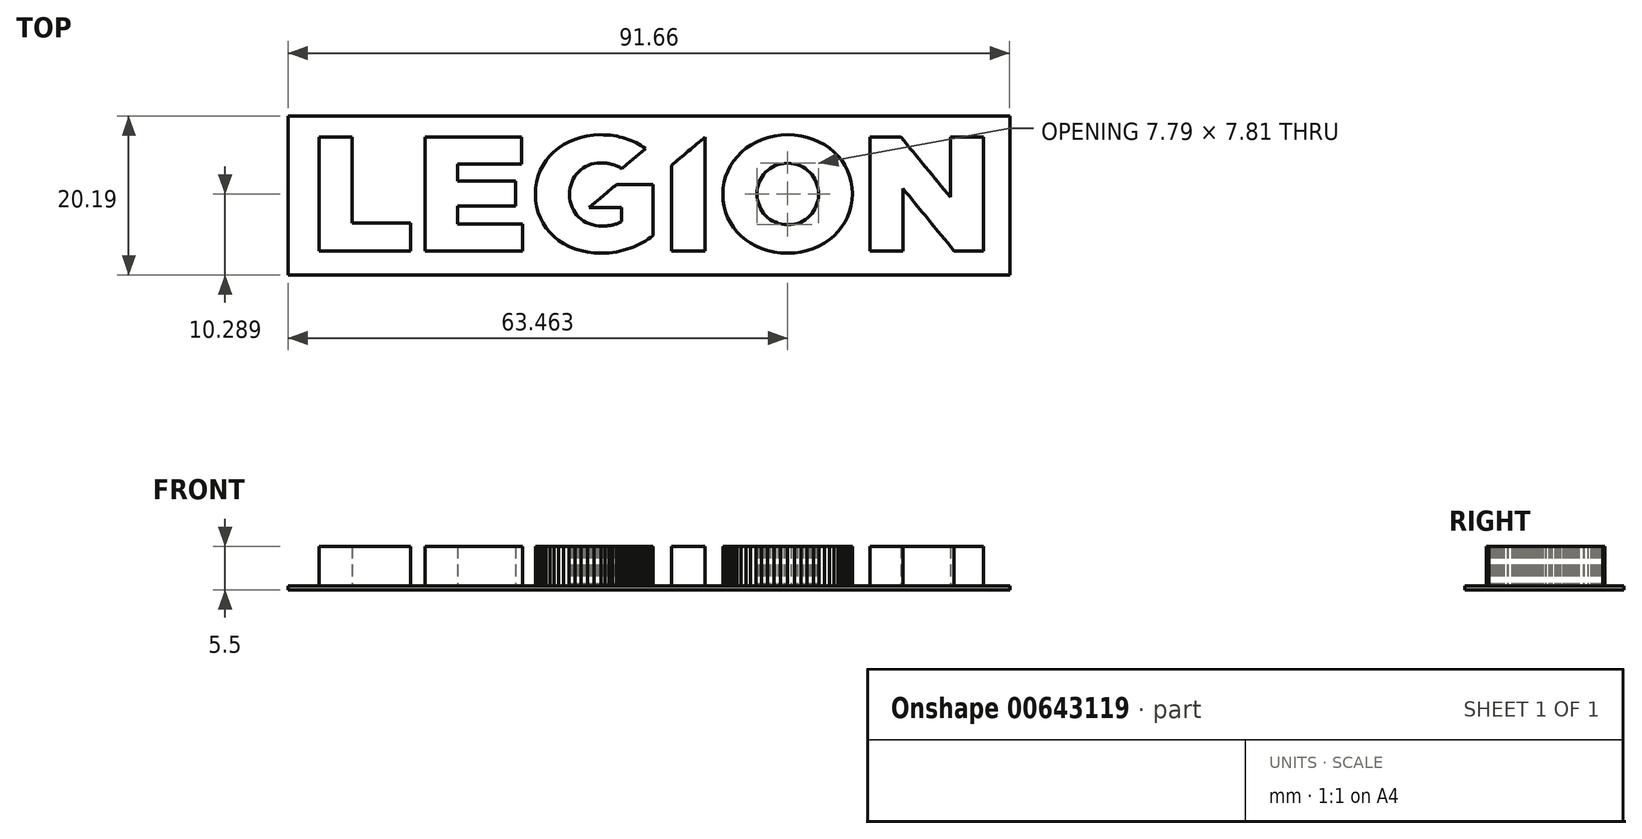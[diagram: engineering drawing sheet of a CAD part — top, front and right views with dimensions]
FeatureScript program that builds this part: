
annotation { "Feature Type Name" : "Feature", "Feature Type Description" : "" }
export const myFeature = defineFeature(function(context is Context, id is Id, definition is map)
    precondition{}
    {
        {
            var Q0;
            Q0=qCreatedBy(makeId("Top.planeOp"),FACE);
            var sketch = newSketch(context, id + "F0", { "sketchPlane" : qUnion([Q0])});
            skLineSegment(sketch, "E0", {"start": v(-42.2, 7.23) * mm, "end": v(-41.94, 7.23) * mm});
            skLineSegment(sketch, "E1", {"start": v(-41.94, 7.23) * mm, "end": v(-41.67, 7.23) * mm});
            skLineSegment(sketch, "E2", {"start": v(-41.67, 7.23) * mm, "end": v(-41.4, 7.23) * mm});
            skLineSegment(sketch, "E3", {"start": v(-41.4, 7.23) * mm, "end": v(-41.14, 7.23) * mm});
            skLineSegment(sketch, "E4", {"start": v(-41.14, 7.23) * mm, "end": v(-40.88, 7.23) * mm});
            skLineSegment(sketch, "E5", {"start": v(-40.88, 7.23) * mm, "end": v(-40.61, 7.23) * mm});
            skLineSegment(sketch, "E6", {"start": v(-40.61, 7.23) * mm, "end": v(-40.35, 7.23) * mm});
            skLineSegment(sketch, "E7", {"start": v(-40.35, 7.23) * mm, "end": v(-40.08, 7.23) * mm});
            skLineSegment(sketch, "E8", {"start": v(-40.08, 7.23) * mm, "end": v(-39.82, 7.23) * mm});
            skLineSegment(sketch, "E9", {"start": v(-39.82, 7.23) * mm, "end": v(-39.55, 7.23) * mm});
            skLineSegment(sketch, "E10", {"start": v(-39.55, 7.23) * mm, "end": v(-39.29, 7.23) * mm});
            skLineSegment(sketch, "E11", {"start": v(-39.29, 7.23) * mm, "end": v(-39.02, 7.23) * mm});
            skLineSegment(sketch, "E12", {"start": v(-39.02, 7.23) * mm, "end": v(-38.76, 7.23) * mm});
            skLineSegment(sketch, "E13", {"start": v(-38.76, 7.23) * mm, "end": v(-38.5, 7.23) * mm});
            skLineSegment(sketch, "E14", {"start": v(-38.5, 7.23) * mm, "end": v(-38.23, 7.23) * mm});
            skLineSegment(sketch, "E15", {"start": v(-38.23, 7.23) * mm, "end": v(-37.97, 7.23) * mm});
            skLineSegment(sketch, "E16", {"start": v(-37.97, 7.23) * mm, "end": v(-37.97, 6.55) * mm});
            skLineSegment(sketch, "E17", {"start": v(-37.97, 6.55) * mm, "end": v(-37.97, 5.86) * mm});
            skLineSegment(sketch, "E18", {"start": v(-37.97, 5.86) * mm, "end": v(-37.97, 5.18) * mm});
            skLineSegment(sketch, "E19", {"start": v(-37.97, 5.18) * mm, "end": v(-37.97, 4.5) * mm});
            skLineSegment(sketch, "E20", {"start": v(-37.97, 4.5) * mm, "end": v(-37.97, 3.81) * mm});
            skLineSegment(sketch, "E21", {"start": v(-37.97, 3.81) * mm, "end": v(-37.97, 3.13) * mm});
            skLineSegment(sketch, "E22", {"start": v(-37.97, 3.13) * mm, "end": v(-37.97, 2.44) * mm});
            skLineSegment(sketch, "E23", {"start": v(-37.97, 2.44) * mm, "end": v(-37.97, 1.76) * mm});
            skLineSegment(sketch, "E24", {"start": v(-37.97, 1.76) * mm, "end": v(-37.97, 1.07) * mm});
            skLineSegment(sketch, "E25", {"start": v(-37.97, 1.07) * mm, "end": v(-37.97, 0.39) * mm});
            skLineSegment(sketch, "E26", {"start": v(-37.97, 0.39) * mm, "end": v(-37.97, -0.3) * mm});
            skLineSegment(sketch, "E27", {"start": v(-37.97, -0.3) * mm, "end": v(-37.97, -0.98) * mm});
            skLineSegment(sketch, "E28", {"start": v(-37.97, -0.98) * mm, "end": v(-37.97, -1.67) * mm});
            skLineSegment(sketch, "E29", {"start": v(-37.97, -1.67) * mm, "end": v(-37.97, -2.35) * mm});
            skLineSegment(sketch, "E30", {"start": v(-37.97, -2.35) * mm, "end": v(-37.97, -3.04) * mm});
            skLineSegment(sketch, "E31", {"start": v(-37.97, -3.04) * mm, "end": v(-37.97, -3.72) * mm});
            skLineSegment(sketch, "E32", {"start": v(-37.97, -3.72) * mm, "end": v(-37.5, -3.72) * mm});
            skLineSegment(sketch, "E33", {"start": v(-37.5, -3.72) * mm, "end": v(-37.04, -3.72) * mm});
            skLineSegment(sketch, "E34", {"start": v(-37.04, -3.72) * mm, "end": v(-36.58, -3.72) * mm});
            skLineSegment(sketch, "E35", {"start": v(-36.58, -3.72) * mm, "end": v(-36.12, -3.72) * mm});
            skLineSegment(sketch, "E36", {"start": v(-36.12, -3.72) * mm, "end": v(-35.65, -3.72) * mm});
            skLineSegment(sketch, "E37", {"start": v(-35.65, -3.72) * mm, "end": v(-35.2, -3.72) * mm});
            skLineSegment(sketch, "E38", {"start": v(-35.2, -3.72) * mm, "end": v(-34.73, -3.72) * mm});
            skLineSegment(sketch, "E39", {"start": v(-34.73, -3.72) * mm, "end": v(-34.27, -3.72) * mm});
            skLineSegment(sketch, "E40", {"start": v(-34.27, -3.72) * mm, "end": v(-33.8, -3.72) * mm});
            skLineSegment(sketch, "E41", {"start": v(-33.8, -3.72) * mm, "end": v(-33.34, -3.72) * mm});
            skLineSegment(sketch, "E42", {"start": v(-33.34, -3.72) * mm, "end": v(-32.88, -3.72) * mm});
            skLineSegment(sketch, "E43", {"start": v(-32.88, -3.72) * mm, "end": v(-32.42, -3.72) * mm});
            skLineSegment(sketch, "E44", {"start": v(-32.42, -3.72) * mm, "end": v(-31.95, -3.72) * mm});
            skLineSegment(sketch, "E45", {"start": v(-31.95, -3.72) * mm, "end": v(-31.5, -3.72) * mm});
            skLineSegment(sketch, "E46", {"start": v(-31.5, -3.72) * mm, "end": v(-31.03, -3.72) * mm});
            skLineSegment(sketch, "E47", {"start": v(-31.03, -3.72) * mm, "end": v(-30.57, -3.72) * mm});
            skLineSegment(sketch, "E48", {"start": v(-30.57, -3.72) * mm, "end": v(-30.57, -3.94) * mm});
            skLineSegment(sketch, "E49", {"start": v(-30.57, -3.94) * mm, "end": v(-30.57, -4.16) * mm});
            skLineSegment(sketch, "E50", {"start": v(-30.57, -4.16) * mm, "end": v(-30.57, -4.38) * mm});
            skLineSegment(sketch, "E51", {"start": v(-30.57, -4.38) * mm, "end": v(-30.57, -4.6) * mm});
            skLineSegment(sketch, "E52", {"start": v(-30.57, -4.6) * mm, "end": v(-30.57, -4.82) * mm});
            skLineSegment(sketch, "E53", {"start": v(-30.57, -4.82) * mm, "end": v(-30.57, -5.04) * mm});
            skLineSegment(sketch, "E54", {"start": v(-30.57, -5.04) * mm, "end": v(-30.57, -5.26) * mm});
            skLineSegment(sketch, "E55", {"start": v(-30.57, -5.26) * mm, "end": v(-30.57, -5.48) * mm});
            skLineSegment(sketch, "E56", {"start": v(-30.57, -5.48) * mm, "end": v(-30.57, -5.7) * mm});
            skLineSegment(sketch, "E57", {"start": v(-30.57, -5.7) * mm, "end": v(-30.57, -5.92) * mm});
            skLineSegment(sketch, "E58", {"start": v(-30.57, -5.92) * mm, "end": v(-30.57, -6.14) * mm});
            skLineSegment(sketch, "E59", {"start": v(-30.57, -6.14) * mm, "end": v(-30.57, -6.36) * mm});
            skLineSegment(sketch, "E60", {"start": v(-30.57, -6.36) * mm, "end": v(-30.57, -6.58) * mm});
            skLineSegment(sketch, "E61", {"start": v(-30.57, -6.58) * mm, "end": v(-30.57, -6.8) * mm});
            skLineSegment(sketch, "E62", {"start": v(-30.57, -6.8) * mm, "end": v(-30.57, -7.01) * mm});
            skLineSegment(sketch, "E63", {"start": v(-30.57, -7.01) * mm, "end": v(-30.57, -7.23) * mm});
            skLineSegment(sketch, "E64", {"start": v(-30.57, -7.23) * mm, "end": v(-31.3, -7.23) * mm});
            skLineSegment(sketch, "E65", {"start": v(-31.3, -7.23) * mm, "end": v(-32.02, -7.23) * mm});
            skLineSegment(sketch, "E66", {"start": v(-32.02, -7.23) * mm, "end": v(-32.75, -7.23) * mm});
            skLineSegment(sketch, "E67", {"start": v(-32.75, -7.23) * mm, "end": v(-33.47, -7.23) * mm});
            skLineSegment(sketch, "E68", {"start": v(-33.47, -7.23) * mm, "end": v(-34.2, -7.23) * mm});
            skLineSegment(sketch, "E69", {"start": v(-34.2, -7.23) * mm, "end": v(-34.93, -7.23) * mm});
            skLineSegment(sketch, "E70", {"start": v(-34.93, -7.23) * mm, "end": v(-35.66, -7.23) * mm});
            skLineSegment(sketch, "E71", {"start": v(-35.66, -7.23) * mm, "end": v(-36.38, -7.23) * mm});
            skLineSegment(sketch, "E72", {"start": v(-36.38, -7.23) * mm, "end": v(-37.1, -7.23) * mm});
            skLineSegment(sketch, "E73", {"start": v(-37.1, -7.23) * mm, "end": v(-37.84, -7.23) * mm});
            skLineSegment(sketch, "E74", {"start": v(-37.84, -7.23) * mm, "end": v(-38.56, -7.23) * mm});
            skLineSegment(sketch, "E75", {"start": v(-38.56, -7.23) * mm, "end": v(-39.3, -7.23) * mm});
            skLineSegment(sketch, "E76", {"start": v(-39.3, -7.23) * mm, "end": v(-40.02, -7.23) * mm});
            skLineSegment(sketch, "E77", {"start": v(-40.02, -7.23) * mm, "end": v(-40.75, -7.23) * mm});
            skLineSegment(sketch, "E78", {"start": v(-40.75, -7.23) * mm, "end": v(-41.47, -7.23) * mm});
            skLineSegment(sketch, "E79", {"start": v(-41.47, -7.23) * mm, "end": v(-42.2, -7.23) * mm});
            skLineSegment(sketch, "E80", {"start": v(-42.2, -7.23) * mm, "end": v(-42.2, -6.33) * mm});
            skLineSegment(sketch, "E81", {"start": v(-42.2, -6.33) * mm, "end": v(-42.2, -5.43) * mm});
            skLineSegment(sketch, "E82", {"start": v(-42.2, -5.43) * mm, "end": v(-42.2, -4.52) * mm});
            skLineSegment(sketch, "E83", {"start": v(-42.2, -4.52) * mm, "end": v(-42.2, -3.62) * mm});
            skLineSegment(sketch, "E84", {"start": v(-42.2, -3.62) * mm, "end": v(-42.2, -2.71) * mm});
            skLineSegment(sketch, "E85", {"start": v(-42.2, -2.71) * mm, "end": v(-42.2, -1.8) * mm});
            skLineSegment(sketch, "E86", {"start": v(-42.2, -1.8) * mm, "end": v(-42.2, -0.9) * mm});
            skLineSegment(sketch, "E87", {"start": v(-42.2, -0.9) * mm, "end": v(-42.2, 0) * mm});
            skLineSegment(sketch, "E88", {"start": v(-42.2, 0) * mm, "end": v(-42.2, 0.9) * mm});
            skLineSegment(sketch, "E89", {"start": v(-42.2, 0.9) * mm, "end": v(-42.2, 1.8) * mm});
            skLineSegment(sketch, "E90", {"start": v(-42.2, 1.8) * mm, "end": v(-42.2, 2.71) * mm});
            skLineSegment(sketch, "E91", {"start": v(-42.2, 2.71) * mm, "end": v(-42.2, 3.62) * mm});
            skLineSegment(sketch, "E92", {"start": v(-42.2, 3.62) * mm, "end": v(-42.2, 4.52) * mm});
            skLineSegment(sketch, "E93", {"start": v(-42.2, 4.52) * mm, "end": v(-42.2, 5.43) * mm});
            skLineSegment(sketch, "E94", {"start": v(-42.2, 5.43) * mm, "end": v(-42.2, 6.33) * mm});
            skLineSegment(sketch, "E95", {"start": v(-42.2, 6.33) * mm, "end": v(-42.2, 7.23) * mm});
            skLineSegment(sketch, "E96", {"start": v(-28.75, 7.23) * mm, "end": v(-27.98, 7.23) * mm});
            skLineSegment(sketch, "E97", {"start": v(-27.98, 7.23) * mm, "end": v(-27.22, 7.23) * mm});
            skLineSegment(sketch, "E98", {"start": v(-27.22, 7.23) * mm, "end": v(-26.45, 7.23) * mm});
            skLineSegment(sketch, "E99", {"start": v(-26.45, 7.23) * mm, "end": v(-25.68, 7.23) * mm});
            skLineSegment(sketch, "E100", {"start": v(-25.68, 7.23) * mm, "end": v(-24.91, 7.23) * mm});
            skLineSegment(sketch, "E101", {"start": v(-24.91, 7.23) * mm, "end": v(-24.14, 7.23) * mm});
            skLineSegment(sketch, "E102", {"start": v(-24.14, 7.23) * mm, "end": v(-23.37, 7.23) * mm});
            skLineSegment(sketch, "E103", {"start": v(-23.37, 7.23) * mm, "end": v(-22.6, 7.23) * mm});
            skLineSegment(sketch, "E104", {"start": v(-22.6, 7.23) * mm, "end": v(-21.84, 7.23) * mm});
            skLineSegment(sketch, "E105", {"start": v(-21.84, 7.23) * mm, "end": v(-21.07, 7.23) * mm});
            skLineSegment(sketch, "E106", {"start": v(-21.07, 7.23) * mm, "end": v(-20.3, 7.23) * mm});
            skLineSegment(sketch, "E107", {"start": v(-20.3, 7.23) * mm, "end": v(-19.53, 7.23) * mm});
            skLineSegment(sketch, "E108", {"start": v(-19.53, 7.23) * mm, "end": v(-18.76, 7.23) * mm});
            skLineSegment(sketch, "E109", {"start": v(-18.76, 7.23) * mm, "end": v(-18, 7.23) * mm});
            skLineSegment(sketch, "E110", {"start": v(-18, 7.23) * mm, "end": v(-17.23, 7.23) * mm});
            skLineSegment(sketch, "E111", {"start": v(-17.23, 7.23) * mm, "end": v(-16.46, 7.23) * mm});
            skLineSegment(sketch, "E112", {"start": v(-16.46, 7.23) * mm, "end": v(-16.46, 7.02) * mm});
            skLineSegment(sketch, "E113", {"start": v(-16.46, 7.02) * mm, "end": v(-16.46, 6.8) * mm});
            skLineSegment(sketch, "E114", {"start": v(-16.46, 6.8) * mm, "end": v(-16.46, 6.6) * mm});
            skLineSegment(sketch, "E115", {"start": v(-16.46, 6.6) * mm, "end": v(-16.46, 6.38) * mm});
            skLineSegment(sketch, "E116", {"start": v(-16.46, 6.38) * mm, "end": v(-16.46, 6.17) * mm});
            skLineSegment(sketch, "E117", {"start": v(-16.46, 6.17) * mm, "end": v(-16.46, 5.96) * mm});
            skLineSegment(sketch, "E118", {"start": v(-16.46, 5.96) * mm, "end": v(-16.46, 5.74) * mm});
            skLineSegment(sketch, "E119", {"start": v(-16.46, 5.74) * mm, "end": v(-16.46, 5.53) * mm});
            skLineSegment(sketch, "E120", {"start": v(-16.46, 5.53) * mm, "end": v(-16.46, 5.32) * mm});
            skLineSegment(sketch, "E121", {"start": v(-16.46, 5.32) * mm, "end": v(-16.46, 5.1) * mm});
            skLineSegment(sketch, "E122", {"start": v(-16.46, 5.1) * mm, "end": v(-16.46, 4.89) * mm});
            skLineSegment(sketch, "E123", {"start": v(-16.46, 4.89) * mm, "end": v(-16.46, 4.68) * mm});
            skLineSegment(sketch, "E124", {"start": v(-16.46, 4.68) * mm, "end": v(-16.46, 4.46) * mm});
            skLineSegment(sketch, "E125", {"start": v(-16.46, 4.46) * mm, "end": v(-16.46, 4.25) * mm});
            skLineSegment(sketch, "E126", {"start": v(-16.46, 4.25) * mm, "end": v(-16.46, 4.04) * mm});
            skLineSegment(sketch, "E127", {"start": v(-16.46, 4.04) * mm, "end": v(-16.46, 3.82) * mm});
            skLineSegment(sketch, "E128", {"start": v(-16.46, 3.82) * mm, "end": v(-16.97, 3.82) * mm});
            skLineSegment(sketch, "E129", {"start": v(-16.97, 3.82) * mm, "end": v(-17.47, 3.82) * mm});
            skLineSegment(sketch, "E130", {"start": v(-17.47, 3.82) * mm, "end": v(-17.98, 3.82) * mm});
            skLineSegment(sketch, "E131", {"start": v(-17.98, 3.82) * mm, "end": v(-18.49, 3.82) * mm});
            skLineSegment(sketch, "E132", {"start": v(-18.49, 3.82) * mm, "end": v(-19, 3.82) * mm});
            skLineSegment(sketch, "E133", {"start": v(-19, 3.82) * mm, "end": v(-19.5, 3.82) * mm});
            skLineSegment(sketch, "E134", {"start": v(-19.5, 3.82) * mm, "end": v(-20, 3.82) * mm});
            skLineSegment(sketch, "E135", {"start": v(-20, 3.82) * mm, "end": v(-20.51, 3.82) * mm});
            skLineSegment(sketch, "E136", {"start": v(-20.51, 3.82) * mm, "end": v(-21.02, 3.82) * mm});
            skLineSegment(sketch, "E137", {"start": v(-21.02, 3.82) * mm, "end": v(-21.52, 3.82) * mm});
            skLineSegment(sketch, "E138", {"start": v(-21.52, 3.82) * mm, "end": v(-22.03, 3.82) * mm});
            skLineSegment(sketch, "E139", {"start": v(-22.03, 3.82) * mm, "end": v(-22.54, 3.82) * mm});
            skLineSegment(sketch, "E140", {"start": v(-22.54, 3.82) * mm, "end": v(-23.04, 3.82) * mm});
            skLineSegment(sketch, "E141", {"start": v(-23.04, 3.82) * mm, "end": v(-23.55, 3.82) * mm});
            skLineSegment(sketch, "E142", {"start": v(-23.55, 3.82) * mm, "end": v(-24.06, 3.82) * mm});
            skLineSegment(sketch, "E143", {"start": v(-24.06, 3.82) * mm, "end": v(-24.56, 3.82) * mm});
            skLineSegment(sketch, "E144", {"start": v(-24.56, 3.82) * mm, "end": v(-24.56, 3.69) * mm});
            skLineSegment(sketch, "E145", {"start": v(-24.56, 3.69) * mm, "end": v(-24.56, 3.55) * mm});
            skLineSegment(sketch, "E146", {"start": v(-24.56, 3.55) * mm, "end": v(-24.56, 3.41) * mm});
            skLineSegment(sketch, "E147", {"start": v(-24.56, 3.41) * mm, "end": v(-24.56, 3.28) * mm});
            skLineSegment(sketch, "E148", {"start": v(-24.56, 3.28) * mm, "end": v(-24.56, 3.14) * mm});
            skLineSegment(sketch, "E149", {"start": v(-24.56, 3.14) * mm, "end": v(-24.56, 3) * mm});
            skLineSegment(sketch, "E150", {"start": v(-24.56, 3) * mm, "end": v(-24.56, 2.87) * mm});
            skLineSegment(sketch, "E151", {"start": v(-24.56, 2.87) * mm, "end": v(-24.56, 2.73) * mm});
            skLineSegment(sketch, "E152", {"start": v(-24.56, 2.73) * mm, "end": v(-24.56, 2.6) * mm});
            skLineSegment(sketch, "E153", {"start": v(-24.56, 2.6) * mm, "end": v(-24.56, 2.45) * mm});
            skLineSegment(sketch, "E154", {"start": v(-24.56, 2.45) * mm, "end": v(-24.56, 2.32) * mm});
            skLineSegment(sketch, "E155", {"start": v(-24.56, 2.32) * mm, "end": v(-24.56, 2.18) * mm});
            skLineSegment(sketch, "E156", {"start": v(-24.56, 2.18) * mm, "end": v(-24.56, 2.04) * mm});
            skLineSegment(sketch, "E157", {"start": v(-24.56, 2.04) * mm, "end": v(-24.56, 1.9) * mm});
            skLineSegment(sketch, "E158", {"start": v(-24.56, 1.9) * mm, "end": v(-24.56, 1.77) * mm});
            skLineSegment(sketch, "E159", {"start": v(-24.56, 1.77) * mm, "end": v(-24.56, 1.63) * mm});
            skLineSegment(sketch, "E160", {"start": v(-24.56, 1.63) * mm, "end": v(-24.1, 1.63) * mm});
            skLineSegment(sketch, "E161", {"start": v(-24.1, 1.63) * mm, "end": v(-23.64, 1.63) * mm});
            skLineSegment(sketch, "E162", {"start": v(-23.64, 1.63) * mm, "end": v(-23.19, 1.63) * mm});
            skLineSegment(sketch, "E163", {"start": v(-23.19, 1.63) * mm, "end": v(-22.73, 1.63) * mm});
            skLineSegment(sketch, "E164", {"start": v(-22.73, 1.63) * mm, "end": v(-22.27, 1.63) * mm});
            skLineSegment(sketch, "E165", {"start": v(-22.27, 1.63) * mm, "end": v(-21.81, 1.63) * mm});
            skLineSegment(sketch, "E166", {"start": v(-21.81, 1.63) * mm, "end": v(-21.35, 1.63) * mm});
            skLineSegment(sketch, "E167", {"start": v(-21.35, 1.63) * mm, "end": v(-20.9, 1.63) * mm});
            skLineSegment(sketch, "E168", {"start": v(-20.9, 1.63) * mm, "end": v(-20.43, 1.63) * mm});
            skLineSegment(sketch, "E169", {"start": v(-20.43, 1.63) * mm, "end": v(-19.98, 1.63) * mm});
            skLineSegment(sketch, "E170", {"start": v(-19.98, 1.63) * mm, "end": v(-19.52, 1.63) * mm});
            skLineSegment(sketch, "E171", {"start": v(-19.52, 1.63) * mm, "end": v(-19.06, 1.63) * mm});
            skLineSegment(sketch, "E172", {"start": v(-19.06, 1.63) * mm, "end": v(-18.6, 1.63) * mm});
            skLineSegment(sketch, "E173", {"start": v(-18.6, 1.63) * mm, "end": v(-18.14, 1.63) * mm});
            skLineSegment(sketch, "E174", {"start": v(-18.14, 1.63) * mm, "end": v(-17.68, 1.63) * mm});
            skLineSegment(sketch, "E175", {"start": v(-17.68, 1.63) * mm, "end": v(-17.23, 1.63) * mm});
            skLineSegment(sketch, "E176", {"start": v(-17.23, 1.63) * mm, "end": v(-17.23, 1.44) * mm});
            skLineSegment(sketch, "E177", {"start": v(-17.23, 1.44) * mm, "end": v(-17.23, 1.24) * mm});
            skLineSegment(sketch, "E178", {"start": v(-17.23, 1.24) * mm, "end": v(-17.23, 1.04) * mm});
            skLineSegment(sketch, "E179", {"start": v(-17.23, 1.04) * mm, "end": v(-17.23, 0.84) * mm});
            skLineSegment(sketch, "E180", {"start": v(-17.23, 0.84) * mm, "end": v(-17.23, 0.64) * mm});
            skLineSegment(sketch, "E181", {"start": v(-17.23, 0.64) * mm, "end": v(-17.23, 0.45) * mm});
            skLineSegment(sketch, "E182", {"start": v(-17.23, 0.45) * mm, "end": v(-17.23, 0.25) * mm});
            skLineSegment(sketch, "E183", {"start": v(-17.23, 0.25) * mm, "end": v(-17.23, 0.05) * mm});
            skLineSegment(sketch, "E184", {"start": v(-17.23, 0.05) * mm, "end": v(-17.23, -0.15) * mm});
            skLineSegment(sketch, "E185", {"start": v(-17.23, -0.15) * mm, "end": v(-17.23, -0.34) * mm});
            skLineSegment(sketch, "E186", {"start": v(-17.23, -0.34) * mm, "end": v(-17.23, -0.54) * mm});
            skLineSegment(sketch, "E187", {"start": v(-17.23, -0.54) * mm, "end": v(-17.23, -0.74) * mm});
            skLineSegment(sketch, "E188", {"start": v(-17.23, -0.74) * mm, "end": v(-17.23, -0.94) * mm});
            skLineSegment(sketch, "E189", {"start": v(-17.23, -0.94) * mm, "end": v(-17.23, -1.13) * mm});
            skLineSegment(sketch, "E190", {"start": v(-17.23, -1.13) * mm, "end": v(-17.23, -1.33) * mm});
            skLineSegment(sketch, "E191", {"start": v(-17.23, -1.33) * mm, "end": v(-17.23, -1.53) * mm});
            skLineSegment(sketch, "E192", {"start": v(-17.23, -1.53) * mm, "end": v(-17.68, -1.53) * mm});
            skLineSegment(sketch, "E193", {"start": v(-17.68, -1.53) * mm, "end": v(-18.14, -1.53) * mm});
            skLineSegment(sketch, "E194", {"start": v(-18.14, -1.53) * mm, "end": v(-18.6, -1.53) * mm});
            skLineSegment(sketch, "E195", {"start": v(-18.6, -1.53) * mm, "end": v(-19.06, -1.53) * mm});
            skLineSegment(sketch, "E196", {"start": v(-19.06, -1.53) * mm, "end": v(-19.52, -1.53) * mm});
            skLineSegment(sketch, "E197", {"start": v(-19.52, -1.53) * mm, "end": v(-19.98, -1.53) * mm});
            skLineSegment(sketch, "E198", {"start": v(-19.98, -1.53) * mm, "end": v(-20.43, -1.53) * mm});
            skLineSegment(sketch, "E199", {"start": v(-20.43, -1.53) * mm, "end": v(-20.9, -1.53) * mm});
            skLineSegment(sketch, "E200", {"start": v(-20.9, -1.53) * mm, "end": v(-21.35, -1.53) * mm});
            skLineSegment(sketch, "E201", {"start": v(-21.35, -1.53) * mm, "end": v(-21.81, -1.53) * mm});
            skLineSegment(sketch, "E202", {"start": v(-21.81, -1.53) * mm, "end": v(-22.27, -1.53) * mm});
            skLineSegment(sketch, "E203", {"start": v(-22.27, -1.53) * mm, "end": v(-22.73, -1.53) * mm});
            skLineSegment(sketch, "E204", {"start": v(-22.73, -1.53) * mm, "end": v(-23.19, -1.53) * mm});
            skLineSegment(sketch, "E205", {"start": v(-23.19, -1.53) * mm, "end": v(-23.64, -1.53) * mm});
            skLineSegment(sketch, "E206", {"start": v(-23.64, -1.53) * mm, "end": v(-24.1, -1.53) * mm});
            skLineSegment(sketch, "E207", {"start": v(-24.1, -1.53) * mm, "end": v(-24.56, -1.53) * mm});
            skLineSegment(sketch, "E208", {"start": v(-24.56, -1.53) * mm, "end": v(-24.56, -1.67) * mm});
            skLineSegment(sketch, "E209", {"start": v(-24.56, -1.67) * mm, "end": v(-24.56, -1.82) * mm});
            skLineSegment(sketch, "E210", {"start": v(-24.56, -1.82) * mm, "end": v(-24.56, -1.96) * mm});
            skLineSegment(sketch, "E211", {"start": v(-24.56, -1.96) * mm, "end": v(-24.56, -2.1) * mm});
            skLineSegment(sketch, "E212", {"start": v(-24.56, -2.1) * mm, "end": v(-24.56, -2.25) * mm});
            skLineSegment(sketch, "E213", {"start": v(-24.56, -2.25) * mm, "end": v(-24.56, -2.39) * mm});
            skLineSegment(sketch, "E214", {"start": v(-24.56, -2.39) * mm, "end": v(-24.56, -2.53) * mm});
            skLineSegment(sketch, "E215", {"start": v(-24.56, -2.53) * mm, "end": v(-24.56, -2.68) * mm});
            skLineSegment(sketch, "E216", {"start": v(-24.56, -2.68) * mm, "end": v(-24.56, -2.82) * mm});
            skLineSegment(sketch, "E217", {"start": v(-24.56, -2.82) * mm, "end": v(-24.56, -2.96) * mm});
            skLineSegment(sketch, "E218", {"start": v(-24.56, -2.96) * mm, "end": v(-24.56, -3.1) * mm});
            skLineSegment(sketch, "E219", {"start": v(-24.56, -3.1) * mm, "end": v(-24.56, -3.25) * mm});
            skLineSegment(sketch, "E220", {"start": v(-24.56, -3.25) * mm, "end": v(-24.56, -3.4) * mm});
            skLineSegment(sketch, "E221", {"start": v(-24.56, -3.4) * mm, "end": v(-24.56, -3.54) * mm});
            skLineSegment(sketch, "E222", {"start": v(-24.56, -3.54) * mm, "end": v(-24.56, -3.68) * mm});
            skLineSegment(sketch, "E223", {"start": v(-24.56, -3.68) * mm, "end": v(-24.56, -3.82) * mm});
            skLineSegment(sketch, "E224", {"start": v(-24.56, -3.82) * mm, "end": v(-24.05, -3.82) * mm});
            skLineSegment(sketch, "E225", {"start": v(-24.05, -3.82) * mm, "end": v(-23.54, -3.82) * mm});
            skLineSegment(sketch, "E226", {"start": v(-23.54, -3.82) * mm, "end": v(-23.02, -3.82) * mm});
            skLineSegment(sketch, "E227", {"start": v(-23.02, -3.82) * mm, "end": v(-22.5, -3.82) * mm});
            skLineSegment(sketch, "E228", {"start": v(-22.5, -3.82) * mm, "end": v(-22, -3.82) * mm});
            skLineSegment(sketch, "E229", {"start": v(-22, -3.82) * mm, "end": v(-21.48, -3.82) * mm});
            skLineSegment(sketch, "E230", {"start": v(-21.48, -3.82) * mm, "end": v(-20.97, -3.82) * mm});
            skLineSegment(sketch, "E231", {"start": v(-20.97, -3.82) * mm, "end": v(-20.46, -3.82) * mm});
            skLineSegment(sketch, "E232", {"start": v(-20.46, -3.82) * mm, "end": v(-19.94, -3.82) * mm});
            skLineSegment(sketch, "E233", {"start": v(-19.94, -3.82) * mm, "end": v(-19.43, -3.82) * mm});
            skLineSegment(sketch, "E234", {"start": v(-19.43, -3.82) * mm, "end": v(-18.92, -3.82) * mm});
            skLineSegment(sketch, "E235", {"start": v(-18.92, -3.82) * mm, "end": v(-18.4, -3.82) * mm});
            skLineSegment(sketch, "E236", {"start": v(-18.4, -3.82) * mm, "end": v(-17.9, -3.82) * mm});
            skLineSegment(sketch, "E237", {"start": v(-17.9, -3.82) * mm, "end": v(-17.38, -3.82) * mm});
            skLineSegment(sketch, "E238", {"start": v(-17.38, -3.82) * mm, "end": v(-16.87, -3.82) * mm});
            skLineSegment(sketch, "E239", {"start": v(-16.87, -3.82) * mm, "end": v(-16.35, -3.82) * mm});
            skLineSegment(sketch, "E240", {"start": v(-16.35, -3.82) * mm, "end": v(-16.35, -4.04) * mm});
            skLineSegment(sketch, "E241", {"start": v(-16.35, -4.04) * mm, "end": v(-16.35, -4.25) * mm});
            skLineSegment(sketch, "E242", {"start": v(-16.35, -4.25) * mm, "end": v(-16.35, -4.46) * mm});
            skLineSegment(sketch, "E243", {"start": v(-16.35, -4.46) * mm, "end": v(-16.35, -4.68) * mm});
            skLineSegment(sketch, "E244", {"start": v(-16.35, -4.68) * mm, "end": v(-16.35, -4.89) * mm});
            skLineSegment(sketch, "E245", {"start": v(-16.35, -4.89) * mm, "end": v(-16.35, -5.1) * mm});
            skLineSegment(sketch, "E246", {"start": v(-16.35, -5.1) * mm, "end": v(-16.35, -5.32) * mm});
            skLineSegment(sketch, "E247", {"start": v(-16.35, -5.32) * mm, "end": v(-16.35, -5.53) * mm});
            skLineSegment(sketch, "E248", {"start": v(-16.35, -5.53) * mm, "end": v(-16.35, -5.74) * mm});
            skLineSegment(sketch, "E249", {"start": v(-16.35, -5.74) * mm, "end": v(-16.35, -5.96) * mm});
            skLineSegment(sketch, "E250", {"start": v(-16.35, -5.96) * mm, "end": v(-16.35, -6.17) * mm});
            skLineSegment(sketch, "E251", {"start": v(-16.35, -6.17) * mm, "end": v(-16.35, -6.38) * mm});
            skLineSegment(sketch, "E252", {"start": v(-16.35, -6.38) * mm, "end": v(-16.35, -6.6) * mm});
            skLineSegment(sketch, "E253", {"start": v(-16.35, -6.6) * mm, "end": v(-16.35, -6.8) * mm});
            skLineSegment(sketch, "E254", {"start": v(-16.35, -6.8) * mm, "end": v(-16.35, -7.02) * mm});
            skLineSegment(sketch, "E255", {"start": v(-16.35, -7.02) * mm, "end": v(-16.35, -7.23) * mm});
            skLineSegment(sketch, "E256", {"start": v(-16.35, -7.23) * mm, "end": v(-17.13, -7.23) * mm});
            skLineSegment(sketch, "E257", {"start": v(-17.13, -7.23) * mm, "end": v(-17.9, -7.23) * mm});
            skLineSegment(sketch, "E258", {"start": v(-17.9, -7.23) * mm, "end": v(-18.68, -7.23) * mm});
            skLineSegment(sketch, "E259", {"start": v(-18.68, -7.23) * mm, "end": v(-19.45, -7.23) * mm});
            skLineSegment(sketch, "E260", {"start": v(-19.45, -7.23) * mm, "end": v(-20.23, -7.23) * mm});
            skLineSegment(sketch, "E261", {"start": v(-20.23, -7.23) * mm, "end": v(-21, -7.23) * mm});
            skLineSegment(sketch, "E262", {"start": v(-21, -7.23) * mm, "end": v(-21.78, -7.23) * mm});
            skLineSegment(sketch, "E263", {"start": v(-21.78, -7.23) * mm, "end": v(-22.55, -7.23) * mm});
            skLineSegment(sketch, "E264", {"start": v(-22.55, -7.23) * mm, "end": v(-23.33, -7.23) * mm});
            skLineSegment(sketch, "E265", {"start": v(-23.33, -7.23) * mm, "end": v(-24.1, -7.23) * mm});
            skLineSegment(sketch, "E266", {"start": v(-24.1, -7.23) * mm, "end": v(-24.88, -7.23) * mm});
            skLineSegment(sketch, "E267", {"start": v(-24.88, -7.23) * mm, "end": v(-25.65, -7.23) * mm});
            skLineSegment(sketch, "E268", {"start": v(-25.65, -7.23) * mm, "end": v(-26.43, -7.23) * mm});
            skLineSegment(sketch, "E269", {"start": v(-26.43, -7.23) * mm, "end": v(-27.2, -7.23) * mm});
            skLineSegment(sketch, "E270", {"start": v(-27.2, -7.23) * mm, "end": v(-27.98, -7.23) * mm});
            skLineSegment(sketch, "E271", {"start": v(-27.98, -7.23) * mm, "end": v(-28.75, -7.23) * mm});
            skLineSegment(sketch, "E272", {"start": v(-28.75, -7.23) * mm, "end": v(-28.75, -6.33) * mm});
            skLineSegment(sketch, "E273", {"start": v(-28.75, -6.33) * mm, "end": v(-28.75, -5.43) * mm});
            skLineSegment(sketch, "E274", {"start": v(-28.75, -5.43) * mm, "end": v(-28.75, -4.52) * mm});
            skLineSegment(sketch, "E275", {"start": v(-28.75, -4.52) * mm, "end": v(-28.75, -3.62) * mm});
            skLineSegment(sketch, "E276", {"start": v(-28.75, -3.62) * mm, "end": v(-28.75, -2.71) * mm});
            skLineSegment(sketch, "E277", {"start": v(-28.75, -2.71) * mm, "end": v(-28.75, -1.8) * mm});
            skLineSegment(sketch, "E278", {"start": v(-28.75, -1.8) * mm, "end": v(-28.75, -0.9) * mm});
            skLineSegment(sketch, "E279", {"start": v(-28.75, -0.9) * mm, "end": v(-28.75, 0) * mm});
            skLineSegment(sketch, "E280", {"start": v(-28.75, 0) * mm, "end": v(-28.75, 0.9) * mm});
            skLineSegment(sketch, "E281", {"start": v(-28.75, 0.9) * mm, "end": v(-28.75, 1.8) * mm});
            skLineSegment(sketch, "E282", {"start": v(-28.75, 1.8) * mm, "end": v(-28.75, 2.71) * mm});
            skLineSegment(sketch, "E283", {"start": v(-28.75, 2.71) * mm, "end": v(-28.75, 3.62) * mm});
            skLineSegment(sketch, "E284", {"start": v(-28.75, 3.62) * mm, "end": v(-28.75, 4.52) * mm});
            skLineSegment(sketch, "E285", {"start": v(-28.75, 4.52) * mm, "end": v(-28.75, 5.43) * mm});
            skLineSegment(sketch, "E286", {"start": v(-28.75, 5.43) * mm, "end": v(-28.75, 6.33) * mm});
            skLineSegment(sketch, "E287", {"start": v(-28.75, 6.33) * mm, "end": v(-28.75, 7.23) * mm});
            skLineSegment(sketch, "E288", {"start": v(21.24, -0.04) * mm, "end": v(21.24, -0.04) * mm});
            skLineSegment(sketch, "E289", {"start": v(21.24, -0.04) * mm, "end": v(21.24, -0.03) * mm});
            skLineSegment(sketch, "E290", {"start": v(21.24, -0.03) * mm, "end": v(21.24, -0.03) * mm});
            skLineSegment(sketch, "E291", {"start": v(21.24, -0.03) * mm, "end": v(21.24, -0.02) * mm});
            skLineSegment(sketch, "E292", {"start": v(21.24, -0.02) * mm, "end": v(21.24, -0.02) * mm});
            skLineSegment(sketch, "E293", {"start": v(21.24, -0.02) * mm, "end": v(21.24, -0.01) * mm});
            skLineSegment(sketch, "E294", {"start": v(21.24, -0.01) * mm, "end": v(21.24, -0.01) * mm});
            skLineSegment(sketch, "E295", {"start": v(21.24, -0.01) * mm, "end": v(21.24, 0) * mm});
            skLineSegment(sketch, "E296", {"start": v(21.24, 0) * mm, "end": v(21.24, 0) * mm});
            skLineSegment(sketch, "E297", {"start": v(21.24, 0) * mm, "end": v(21.22, 0.39) * mm});
            skLineSegment(sketch, "E298", {"start": v(21.22, 0.39) * mm, "end": v(21.17, 0.77) * mm});
            skLineSegment(sketch, "E299", {"start": v(21.17, 0.77) * mm, "end": v(21.08, 1.14) * mm});
            skLineSegment(sketch, "E300", {"start": v(21.08, 1.14) * mm, "end": v(20.96, 1.5) * mm});
            skLineSegment(sketch, "E301", {"start": v(20.96, 1.5) * mm, "end": v(20.8, 1.83) * mm});
            skLineSegment(sketch, "E302", {"start": v(20.8, 1.83) * mm, "end": v(20.61, 2.15) * mm});
            skLineSegment(sketch, "E303", {"start": v(20.61, 2.15) * mm, "end": v(20.4, 2.46) * mm});
            skLineSegment(sketch, "E304", {"start": v(20.4, 2.46) * mm, "end": v(20.15, 2.74) * mm});
            skLineSegment(sketch, "E305", {"start": v(20.15, 2.74) * mm, "end": v(19.88, 3) * mm});
            skLineSegment(sketch, "E306", {"start": v(19.88, 3) * mm, "end": v(19.58, 3.22) * mm});
            skLineSegment(sketch, "E307", {"start": v(19.58, 3.22) * mm, "end": v(19.26, 3.42) * mm});
            skLineSegment(sketch, "E308", {"start": v(19.26, 3.42) * mm, "end": v(18.91, 3.59) * mm});
            skLineSegment(sketch, "E309", {"start": v(18.91, 3.59) * mm, "end": v(18.54, 3.72) * mm});
            skLineSegment(sketch, "E310", {"start": v(18.54, 3.72) * mm, "end": v(18.15, 3.82) * mm});
            skLineSegment(sketch, "E311", {"start": v(18.15, 3.82) * mm, "end": v(17.74, 3.88) * mm});
            skLineSegment(sketch, "E312", {"start": v(17.74, 3.88) * mm, "end": v(17.3, 3.9) * mm});
            skLineSegment(sketch, "E313", {"start": v(17.3, 3.9) * mm, "end": v(16.88, 3.89) * mm});
            skLineSegment(sketch, "E314", {"start": v(16.88, 3.89) * mm, "end": v(16.48, 3.83) * mm});
            skLineSegment(sketch, "E315", {"start": v(16.48, 3.83) * mm, "end": v(16.1, 3.73) * mm});
            skLineSegment(sketch, "E316", {"start": v(16.1, 3.73) * mm, "end": v(15.73, 3.6) * mm});
            skLineSegment(sketch, "E317", {"start": v(15.73, 3.6) * mm, "end": v(15.39, 3.43) * mm});
            skLineSegment(sketch, "E318", {"start": v(15.39, 3.43) * mm, "end": v(15.07, 3.23) * mm});
            skLineSegment(sketch, "E319", {"start": v(15.07, 3.23) * mm, "end": v(14.78, 3) * mm});
            skLineSegment(sketch, "E320", {"start": v(14.78, 3) * mm, "end": v(14.51, 2.76) * mm});
            skLineSegment(sketch, "E321", {"start": v(14.51, 2.76) * mm, "end": v(14.27, 2.48) * mm});
            skLineSegment(sketch, "E322", {"start": v(14.27, 2.48) * mm, "end": v(14.06, 2.18) * mm});
            skLineSegment(sketch, "E323", {"start": v(14.06, 2.18) * mm, "end": v(13.88, 1.86) * mm});
            skLineSegment(sketch, "E324", {"start": v(13.88, 1.86) * mm, "end": v(13.73, 1.53) * mm});
            skLineSegment(sketch, "E325", {"start": v(13.73, 1.53) * mm, "end": v(13.6, 1.17) * mm});
            skLineSegment(sketch, "E326", {"start": v(13.6, 1.17) * mm, "end": v(13.52, 0.8) * mm});
            skLineSegment(sketch, "E327", {"start": v(13.52, 0.8) * mm, "end": v(13.46, 0.43) * mm});
            skLineSegment(sketch, "E328", {"start": v(13.46, 0.43) * mm, "end": v(13.45, 0.04) * mm});
            skLineSegment(sketch, "E329", {"start": v(13.45, 0.04) * mm, "end": v(13.45, 0.04) * mm});
            skLineSegment(sketch, "E330", {"start": v(13.45, 0.04) * mm, "end": v(13.45, 0.03) * mm});
            skLineSegment(sketch, "E331", {"start": v(13.45, 0.03) * mm, "end": v(13.45, 0.03) * mm});
            skLineSegment(sketch, "E332", {"start": v(13.45, 0.03) * mm, "end": v(13.45, 0.02) * mm});
            skLineSegment(sketch, "E333", {"start": v(13.45, 0.02) * mm, "end": v(13.45, 0.02) * mm});
            skLineSegment(sketch, "E334", {"start": v(13.45, 0.02) * mm, "end": v(13.45, 0.01) * mm});
            skLineSegment(sketch, "E335", {"start": v(13.45, 0.01) * mm, "end": v(13.45, 0) * mm});
            skLineSegment(sketch, "E336", {"start": v(13.45, 0) * mm, "end": v(13.45, 0) * mm});
            skLineSegment(sketch, "E337", {"start": v(13.45, 0) * mm, "end": v(13.47, -0.39) * mm});
            skLineSegment(sketch, "E338", {"start": v(13.47, -0.39) * mm, "end": v(13.52, -0.77) * mm});
            skLineSegment(sketch, "E339", {"start": v(13.52, -0.77) * mm, "end": v(13.6, -1.14) * mm});
            skLineSegment(sketch, "E340", {"start": v(13.6, -1.14) * mm, "end": v(13.73, -1.5) * mm});
            skLineSegment(sketch, "E341", {"start": v(13.73, -1.5) * mm, "end": v(13.89, -1.83) * mm});
            skLineSegment(sketch, "E342", {"start": v(13.89, -1.83) * mm, "end": v(14.07, -2.15) * mm});
            skLineSegment(sketch, "E343", {"start": v(14.07, -2.15) * mm, "end": v(14.29, -2.46) * mm});
            skLineSegment(sketch, "E344", {"start": v(14.29, -2.46) * mm, "end": v(14.53, -2.74) * mm});
            skLineSegment(sketch, "E345", {"start": v(14.53, -2.74) * mm, "end": v(14.8, -3) * mm});
            skLineSegment(sketch, "E346", {"start": v(14.8, -3) * mm, "end": v(15.1, -3.22) * mm});
            skLineSegment(sketch, "E347", {"start": v(15.1, -3.22) * mm, "end": v(15.42, -3.42) * mm});
            skLineSegment(sketch, "E348", {"start": v(15.42, -3.42) * mm, "end": v(15.77, -3.6) * mm});
            skLineSegment(sketch, "E349", {"start": v(15.77, -3.6) * mm, "end": v(16.14, -3.73) * mm});
            skLineSegment(sketch, "E350", {"start": v(16.14, -3.73) * mm, "end": v(16.52, -3.83) * mm});
            skLineSegment(sketch, "E351", {"start": v(16.52, -3.83) * mm, "end": v(16.93, -3.89) * mm});
            skLineSegment(sketch, "E352", {"start": v(16.93, -3.89) * mm, "end": v(17.35, -3.9) * mm});
            skLineSegment(sketch, "E353", {"start": v(17.35, -3.9) * mm, "end": v(17.78, -3.89) * mm});
            skLineSegment(sketch, "E354", {"start": v(17.78, -3.89) * mm, "end": v(18.2, -3.83) * mm});
            skLineSegment(sketch, "E355", {"start": v(18.2, -3.83) * mm, "end": v(18.58, -3.73) * mm});
            skLineSegment(sketch, "E356", {"start": v(18.58, -3.73) * mm, "end": v(18.95, -3.6) * mm});
            skLineSegment(sketch, "E357", {"start": v(18.95, -3.6) * mm, "end": v(19.3, -3.43) * mm});
            skLineSegment(sketch, "E358", {"start": v(19.3, -3.43) * mm, "end": v(19.61, -3.24) * mm});
            skLineSegment(sketch, "E359", {"start": v(19.61, -3.24) * mm, "end": v(19.9, -3) * mm});
            skLineSegment(sketch, "E360", {"start": v(19.9, -3) * mm, "end": v(20.17, -2.76) * mm});
            skLineSegment(sketch, "E361", {"start": v(20.17, -2.76) * mm, "end": v(20.41, -2.48) * mm});
            skLineSegment(sketch, "E362", {"start": v(20.41, -2.48) * mm, "end": v(20.63, -2.18) * mm});
            skLineSegment(sketch, "E363", {"start": v(20.63, -2.18) * mm, "end": v(20.8, -1.86) * mm});
            skLineSegment(sketch, "E364", {"start": v(20.8, -1.86) * mm, "end": v(20.96, -1.53) * mm});
            skLineSegment(sketch, "E365", {"start": v(20.96, -1.53) * mm, "end": v(21.08, -1.17) * mm});
            skLineSegment(sketch, "E366", {"start": v(21.08, -1.17) * mm, "end": v(21.17, -0.8) * mm});
            skLineSegment(sketch, "E367", {"start": v(21.17, -0.8) * mm, "end": v(21.22, -0.43) * mm});
            skLineSegment(sketch, "E368", {"start": v(21.22, -0.43) * mm, "end": v(21.24, -0.04) * mm});
            skLineSegment(sketch, "E369", {"start": v(9.1, -0.04) * mm, "end": v(9.1, -0.04) * mm});
            skLineSegment(sketch, "E370", {"start": v(9.1, -0.04) * mm, "end": v(9.1, -0.03) * mm});
            skLineSegment(sketch, "E371", {"start": v(9.1, -0.03) * mm, "end": v(9.1, -0.03) * mm});
            skLineSegment(sketch, "E372", {"start": v(9.1, -0.03) * mm, "end": v(9.1, -0.02) * mm});
            skLineSegment(sketch, "E373", {"start": v(9.1, -0.02) * mm, "end": v(9.1, -0.02) * mm});
            skLineSegment(sketch, "E374", {"start": v(9.1, -0.02) * mm, "end": v(9.1, -0.01) * mm});
            skLineSegment(sketch, "E375", {"start": v(9.1, -0.01) * mm, "end": v(9.1, -0.01) * mm});
            skLineSegment(sketch, "E376", {"start": v(9.1, -0.01) * mm, "end": v(9.1, 0) * mm});
            skLineSegment(sketch, "E377", {"start": v(9.1, 0) * mm, "end": v(9.1, 0) * mm});
            skLineSegment(sketch, "E378", {"start": v(9.1, 0) * mm, "end": v(9.14, 0.77) * mm});
            skLineSegment(sketch, "E379", {"start": v(9.14, 0.77) * mm, "end": v(9.26, 1.52) * mm});
            skLineSegment(sketch, "E380", {"start": v(9.26, 1.52) * mm, "end": v(9.46, 2.24) * mm});
            skLineSegment(sketch, "E381", {"start": v(9.46, 2.24) * mm, "end": v(9.73, 2.93) * mm});
            skLineSegment(sketch, "E382", {"start": v(9.73, 2.93) * mm, "end": v(10.07, 3.59) * mm});
            skLineSegment(sketch, "E383", {"start": v(10.07, 3.59) * mm, "end": v(10.47, 4.2) * mm});
            skLineSegment(sketch, "E384", {"start": v(10.47, 4.2) * mm, "end": v(10.94, 4.79) * mm});
            skLineSegment(sketch, "E385", {"start": v(10.94, 4.79) * mm, "end": v(11.46, 5.32) * mm});
            skLineSegment(sketch, "E386", {"start": v(11.46, 5.32) * mm, "end": v(12.04, 5.8) * mm});
            skLineSegment(sketch, "E387", {"start": v(12.04, 5.8) * mm, "end": v(12.67, 6.24) * mm});
            skLineSegment(sketch, "E388", {"start": v(12.67, 6.24) * mm, "end": v(13.35, 6.62) * mm});
            skLineSegment(sketch, "E389", {"start": v(13.35, 6.62) * mm, "end": v(14.08, 6.93) * mm});
            skLineSegment(sketch, "E390", {"start": v(14.08, 6.93) * mm, "end": v(14.84, 7.19) * mm});
            skLineSegment(sketch, "E391", {"start": v(14.84, 7.19) * mm, "end": v(15.65, 7.37) * mm});
            skLineSegment(sketch, "E392", {"start": v(15.65, 7.37) * mm, "end": v(16.48, 7.49) * mm});
            skLineSegment(sketch, "E393", {"start": v(16.48, 7.49) * mm, "end": v(17.35, 7.52) * mm});
            skLineSegment(sketch, "E394", {"start": v(17.35, 7.52) * mm, "end": v(18.22, 7.49) * mm});
            skLineSegment(sketch, "E395", {"start": v(18.22, 7.49) * mm, "end": v(19.06, 7.37) * mm});
            skLineSegment(sketch, "E396", {"start": v(19.06, 7.37) * mm, "end": v(19.86, 7.19) * mm});
            skLineSegment(sketch, "E397", {"start": v(19.86, 7.19) * mm, "end": v(20.63, 6.94) * mm});
            skLineSegment(sketch, "E398", {"start": v(20.63, 6.94) * mm, "end": v(21.35, 6.63) * mm});
            skLineSegment(sketch, "E399", {"start": v(21.35, 6.63) * mm, "end": v(22.02, 6.25) * mm});
            skLineSegment(sketch, "E400", {"start": v(22.02, 6.25) * mm, "end": v(22.65, 5.82) * mm});
            skLineSegment(sketch, "E401", {"start": v(22.65, 5.82) * mm, "end": v(23.23, 5.34) * mm});
            skLineSegment(sketch, "E402", {"start": v(23.23, 5.34) * mm, "end": v(23.75, 4.81) * mm});
            skLineSegment(sketch, "E403", {"start": v(23.75, 4.81) * mm, "end": v(24.21, 4.23) * mm});
            skLineSegment(sketch, "E404", {"start": v(24.21, 4.23) * mm, "end": v(24.61, 3.62) * mm});
            skLineSegment(sketch, "E405", {"start": v(24.61, 3.62) * mm, "end": v(24.94, 2.96) * mm});
            skLineSegment(sketch, "E406", {"start": v(24.94, 2.96) * mm, "end": v(25.21, 2.27) * mm});
            skLineSegment(sketch, "E407", {"start": v(25.21, 2.27) * mm, "end": v(25.4, 1.56) * mm});
            skLineSegment(sketch, "E408", {"start": v(25.4, 1.56) * mm, "end": v(25.52, 0.81) * mm});
            skLineSegment(sketch, "E409", {"start": v(25.52, 0.81) * mm, "end": v(25.56, 0.04) * mm});
            skLineSegment(sketch, "E410", {"start": v(25.56, 0.04) * mm, "end": v(25.56, 0.04) * mm});
            skLineSegment(sketch, "E411", {"start": v(25.56, 0.04) * mm, "end": v(25.56, 0.03) * mm});
            skLineSegment(sketch, "E412", {"start": v(25.56, 0.03) * mm, "end": v(25.56, 0.03) * mm});
            skLineSegment(sketch, "E413", {"start": v(25.56, 0.03) * mm, "end": v(25.56, 0.02) * mm});
            skLineSegment(sketch, "E414", {"start": v(25.56, 0.02) * mm, "end": v(25.56, 0.02) * mm});
            skLineSegment(sketch, "E415", {"start": v(25.56, 0.02) * mm, "end": v(25.56, 0.01) * mm});
            skLineSegment(sketch, "E416", {"start": v(25.56, 0.01) * mm, "end": v(25.56, 0) * mm});
            skLineSegment(sketch, "E417", {"start": v(25.56, 0) * mm, "end": v(25.56, 0) * mm});
            skLineSegment(sketch, "E418", {"start": v(25.56, 0) * mm, "end": v(25.52, -0.77) * mm});
            skLineSegment(sketch, "E419", {"start": v(25.52, -0.77) * mm, "end": v(25.4, -1.52) * mm});
            skLineSegment(sketch, "E420", {"start": v(25.4, -1.52) * mm, "end": v(25.2, -2.24) * mm});
            skLineSegment(sketch, "E421", {"start": v(25.2, -2.24) * mm, "end": v(24.94, -2.93) * mm});
            skLineSegment(sketch, "E422", {"start": v(24.94, -2.93) * mm, "end": v(24.6, -3.59) * mm});
            skLineSegment(sketch, "E423", {"start": v(24.6, -3.59) * mm, "end": v(24.2, -4.2) * mm});
            skLineSegment(sketch, "E424", {"start": v(24.2, -4.2) * mm, "end": v(23.73, -4.79) * mm});
            skLineSegment(sketch, "E425", {"start": v(23.73, -4.79) * mm, "end": v(23.2, -5.32) * mm});
            skLineSegment(sketch, "E426", {"start": v(23.2, -5.32) * mm, "end": v(22.63, -5.8) * mm});
            skLineSegment(sketch, "E427", {"start": v(22.63, -5.8) * mm, "end": v(22, -6.24) * mm});
            skLineSegment(sketch, "E428", {"start": v(22, -6.24) * mm, "end": v(21.31, -6.62) * mm});
            skLineSegment(sketch, "E429", {"start": v(21.31, -6.62) * mm, "end": v(20.59, -6.93) * mm});
            skLineSegment(sketch, "E430", {"start": v(20.59, -6.93) * mm, "end": v(19.82, -7.19) * mm});
            skLineSegment(sketch, "E431", {"start": v(19.82, -7.19) * mm, "end": v(19.02, -7.37) * mm});
            skLineSegment(sketch, "E432", {"start": v(19.02, -7.37) * mm, "end": v(18.18, -7.49) * mm});
            skLineSegment(sketch, "E433", {"start": v(18.18, -7.49) * mm, "end": v(17.3, -7.52) * mm});
            skLineSegment(sketch, "E434", {"start": v(17.3, -7.52) * mm, "end": v(16.44, -7.49) * mm});
            skLineSegment(sketch, "E435", {"start": v(16.44, -7.49) * mm, "end": v(15.6, -7.37) * mm});
            skLineSegment(sketch, "E436", {"start": v(15.6, -7.37) * mm, "end": v(14.8, -7.19) * mm});
            skLineSegment(sketch, "E437", {"start": v(14.8, -7.19) * mm, "end": v(14.04, -6.94) * mm});
            skLineSegment(sketch, "E438", {"start": v(14.04, -6.94) * mm, "end": v(13.32, -6.63) * mm});
            skLineSegment(sketch, "E439", {"start": v(13.32, -6.63) * mm, "end": v(12.64, -6.25) * mm});
            skLineSegment(sketch, "E440", {"start": v(12.64, -6.25) * mm, "end": v(12.01, -5.82) * mm});
            skLineSegment(sketch, "E441", {"start": v(12.01, -5.82) * mm, "end": v(11.44, -5.34) * mm});
            skLineSegment(sketch, "E442", {"start": v(11.44, -5.34) * mm, "end": v(10.92, -4.81) * mm});
            skLineSegment(sketch, "E443", {"start": v(10.92, -4.81) * mm, "end": v(10.46, -4.24) * mm});
            skLineSegment(sketch, "E444", {"start": v(10.46, -4.24) * mm, "end": v(10.06, -3.62) * mm});
            skLineSegment(sketch, "E445", {"start": v(10.06, -3.62) * mm, "end": v(9.72, -2.96) * mm});
            skLineSegment(sketch, "E446", {"start": v(9.72, -2.96) * mm, "end": v(9.46, -2.28) * mm});
            skLineSegment(sketch, "E447", {"start": v(9.46, -2.28) * mm, "end": v(9.26, -1.56) * mm});
            skLineSegment(sketch, "E448", {"start": v(9.26, -1.56) * mm, "end": v(9.14, -0.81) * mm});
            skLineSegment(sketch, "E449", {"start": v(9.14, -0.81) * mm, "end": v(9.1, -0.04) * mm});
            skLineSegment(sketch, "E450", {"start": v(27.77, 7.23) * mm, "end": v(28.02, 7.23) * mm});
            skLineSegment(sketch, "E451", {"start": v(28.02, 7.23) * mm, "end": v(28.26, 7.23) * mm});
            skLineSegment(sketch, "E452", {"start": v(28.26, 7.23) * mm, "end": v(28.51, 7.23) * mm});
            skLineSegment(sketch, "E453", {"start": v(28.51, 7.23) * mm, "end": v(28.76, 7.23) * mm});
            skLineSegment(sketch, "E454", {"start": v(28.76, 7.23) * mm, "end": v(29, 7.23) * mm});
            skLineSegment(sketch, "E455", {"start": v(29, 7.23) * mm, "end": v(29.25, 7.23) * mm});
            skLineSegment(sketch, "E456", {"start": v(29.25, 7.23) * mm, "end": v(29.5, 7.23) * mm});
            skLineSegment(sketch, "E457", {"start": v(29.5, 7.23) * mm, "end": v(29.74, 7.23) * mm});
            skLineSegment(sketch, "E458", {"start": v(29.74, 7.23) * mm, "end": v(30, 7.23) * mm});
            skLineSegment(sketch, "E459", {"start": v(30, 7.23) * mm, "end": v(30.24, 7.23) * mm});
            skLineSegment(sketch, "E460", {"start": v(30.24, 7.23) * mm, "end": v(30.49, 7.23) * mm});
            skLineSegment(sketch, "E461", {"start": v(30.49, 7.23) * mm, "end": v(30.73, 7.23) * mm});
            skLineSegment(sketch, "E462", {"start": v(30.73, 7.23) * mm, "end": v(30.98, 7.23) * mm});
            skLineSegment(sketch, "E463", {"start": v(30.98, 7.23) * mm, "end": v(31.23, 7.23) * mm});
            skLineSegment(sketch, "E464", {"start": v(31.23, 7.23) * mm, "end": v(31.47, 7.23) * mm});
            skLineSegment(sketch, "E465", {"start": v(31.47, 7.23) * mm, "end": v(31.72, 7.23) * mm});
            skLineSegment(sketch, "E466", {"start": v(31.72, 7.23) * mm, "end": v(32.11, 6.76) * mm});
            skLineSegment(sketch, "E467", {"start": v(32.11, 6.76) * mm, "end": v(32.5, 6.28) * mm});
            skLineSegment(sketch, "E468", {"start": v(32.5, 6.28) * mm, "end": v(32.9, 5.8) * mm});
            skLineSegment(sketch, "E469", {"start": v(32.9, 5.8) * mm, "end": v(33.3, 5.32) * mm});
            skLineSegment(sketch, "E470", {"start": v(33.3, 5.32) * mm, "end": v(33.68, 4.84) * mm});
            skLineSegment(sketch, "E471", {"start": v(33.68, 4.84) * mm, "end": v(34.08, 4.37) * mm});
            skLineSegment(sketch, "E472", {"start": v(34.08, 4.37) * mm, "end": v(34.47, 3.89) * mm});
            skLineSegment(sketch, "E473", {"start": v(34.47, 3.89) * mm, "end": v(34.86, 3.41) * mm});
            skLineSegment(sketch, "E474", {"start": v(34.86, 3.41) * mm, "end": v(35.26, 2.93) * mm});
            skLineSegment(sketch, "E475", {"start": v(35.26, 2.93) * mm, "end": v(35.65, 2.45) * mm});
            skLineSegment(sketch, "E476", {"start": v(35.65, 2.45) * mm, "end": v(36.04, 1.98) * mm});
            skLineSegment(sketch, "E477", {"start": v(36.04, 1.98) * mm, "end": v(36.44, 1.5) * mm});
            skLineSegment(sketch, "E478", {"start": v(36.44, 1.5) * mm, "end": v(36.83, 1.02) * mm});
            skLineSegment(sketch, "E479", {"start": v(36.83, 1.02) * mm, "end": v(37.22, 0.54) * mm});
            skLineSegment(sketch, "E480", {"start": v(37.22, 0.54) * mm, "end": v(37.61, 0.06) * mm});
            skLineSegment(sketch, "E481", {"start": v(37.61, 0.06) * mm, "end": v(38, -0.41) * mm});
            skLineSegment(sketch, "E482", {"start": v(38, -0.41) * mm, "end": v(38, 0.06) * mm});
            skLineSegment(sketch, "E483", {"start": v(38, 0.06) * mm, "end": v(38, 0.54) * mm});
            skLineSegment(sketch, "E484", {"start": v(38, 0.54) * mm, "end": v(38, 1.02) * mm});
            skLineSegment(sketch, "E485", {"start": v(38, 1.02) * mm, "end": v(38, 1.5) * mm});
            skLineSegment(sketch, "E486", {"start": v(38, 1.5) * mm, "end": v(38, 1.98) * mm});
            skLineSegment(sketch, "E487", {"start": v(38, 1.98) * mm, "end": v(38, 2.45) * mm});
            skLineSegment(sketch, "E488", {"start": v(38, 2.45) * mm, "end": v(38, 2.93) * mm});
            skLineSegment(sketch, "E489", {"start": v(38, 2.93) * mm, "end": v(38, 3.41) * mm});
            skLineSegment(sketch, "E490", {"start": v(38, 3.41) * mm, "end": v(38, 3.89) * mm});
            skLineSegment(sketch, "E491", {"start": v(38, 3.89) * mm, "end": v(38, 4.37) * mm});
            skLineSegment(sketch, "E492", {"start": v(38, 4.37) * mm, "end": v(38, 4.84) * mm});
            skLineSegment(sketch, "E493", {"start": v(38, 4.84) * mm, "end": v(38, 5.32) * mm});
            skLineSegment(sketch, "E494", {"start": v(38, 5.32) * mm, "end": v(38, 5.8) * mm});
            skLineSegment(sketch, "E495", {"start": v(38, 5.8) * mm, "end": v(38, 6.28) * mm});
            skLineSegment(sketch, "E496", {"start": v(38, 6.28) * mm, "end": v(38, 6.76) * mm});
            skLineSegment(sketch, "E497", {"start": v(38, 6.76) * mm, "end": v(38, 7.23) * mm});
            skLineSegment(sketch, "E498", {"start": v(38, 7.23) * mm, "end": v(38.27, 7.23) * mm});
            skLineSegment(sketch, "E499", {"start": v(38.27, 7.23) * mm, "end": v(38.53, 7.23) * mm});
            skLineSegment(sketch, "E500", {"start": v(38.53, 7.23) * mm, "end": v(38.8, 7.23) * mm});
            skLineSegment(sketch, "E501", {"start": v(38.8, 7.23) * mm, "end": v(39.06, 7.23) * mm});
            skLineSegment(sketch, "E502", {"start": v(39.06, 7.23) * mm, "end": v(39.32, 7.23) * mm});
            skLineSegment(sketch, "E503", {"start": v(39.32, 7.23) * mm, "end": v(39.58, 7.23) * mm});
            skLineSegment(sketch, "E504", {"start": v(39.58, 7.23) * mm, "end": v(39.84, 7.23) * mm});
            skLineSegment(sketch, "E505", {"start": v(39.84, 7.23) * mm, "end": v(40.1, 7.23) * mm});
            skLineSegment(sketch, "E506", {"start": v(40.1, 7.23) * mm, "end": v(40.37, 7.23) * mm});
            skLineSegment(sketch, "E507", {"start": v(40.37, 7.23) * mm, "end": v(40.63, 7.23) * mm});
            skLineSegment(sketch, "E508", {"start": v(40.63, 7.23) * mm, "end": v(40.89, 7.23) * mm});
            skLineSegment(sketch, "E509", {"start": v(40.89, 7.23) * mm, "end": v(41.15, 7.23) * mm});
            skLineSegment(sketch, "E510", {"start": v(41.15, 7.23) * mm, "end": v(41.41, 7.23) * mm});
            skLineSegment(sketch, "E511", {"start": v(41.41, 7.23) * mm, "end": v(41.68, 7.23) * mm});
            skLineSegment(sketch, "E512", {"start": v(41.68, 7.23) * mm, "end": v(41.94, 7.23) * mm});
            skLineSegment(sketch, "E513", {"start": v(41.94, 7.23) * mm, "end": v(42.2, 7.23) * mm});
            skLineSegment(sketch, "E514", {"start": v(42.2, 7.23) * mm, "end": v(42.2, 6.33) * mm});
            skLineSegment(sketch, "E515", {"start": v(42.2, 6.33) * mm, "end": v(42.2, 5.43) * mm});
            skLineSegment(sketch, "E516", {"start": v(42.2, 5.43) * mm, "end": v(42.2, 4.52) * mm});
            skLineSegment(sketch, "E517", {"start": v(42.2, 4.52) * mm, "end": v(42.2, 3.62) * mm});
            skLineSegment(sketch, "E518", {"start": v(42.2, 3.62) * mm, "end": v(42.2, 2.71) * mm});
            skLineSegment(sketch, "E519", {"start": v(42.2, 2.71) * mm, "end": v(42.2, 1.8) * mm});
            skLineSegment(sketch, "E520", {"start": v(42.2, 1.8) * mm, "end": v(42.2, 0.9) * mm});
            skLineSegment(sketch, "E521", {"start": v(42.2, 0.9) * mm, "end": v(42.2, 0) * mm});
            skLineSegment(sketch, "E522", {"start": v(42.2, 0) * mm, "end": v(42.2, -0.9) * mm});
            skLineSegment(sketch, "E523", {"start": v(42.2, -0.9) * mm, "end": v(42.2, -1.8) * mm});
            skLineSegment(sketch, "E524", {"start": v(42.2, -1.8) * mm, "end": v(42.2, -2.71) * mm});
            skLineSegment(sketch, "E525", {"start": v(42.2, -2.71) * mm, "end": v(42.2, -3.62) * mm});
            skLineSegment(sketch, "E526", {"start": v(42.2, -3.62) * mm, "end": v(42.2, -4.52) * mm});
            skLineSegment(sketch, "E527", {"start": v(42.2, -4.52) * mm, "end": v(42.2, -5.43) * mm});
            skLineSegment(sketch, "E528", {"start": v(42.2, -5.43) * mm, "end": v(42.2, -6.33) * mm});
            skLineSegment(sketch, "E529", {"start": v(42.2, -6.33) * mm, "end": v(42.2, -7.23) * mm});
            skLineSegment(sketch, "E530", {"start": v(42.2, -7.23) * mm, "end": v(41.97, -7.23) * mm});
            skLineSegment(sketch, "E531", {"start": v(41.97, -7.23) * mm, "end": v(41.74, -7.23) * mm});
            skLineSegment(sketch, "E532", {"start": v(41.74, -7.23) * mm, "end": v(41.5, -7.23) * mm});
            skLineSegment(sketch, "E533", {"start": v(41.5, -7.23) * mm, "end": v(41.27, -7.23) * mm});
            skLineSegment(sketch, "E534", {"start": v(41.27, -7.23) * mm, "end": v(41.04, -7.23) * mm});
            skLineSegment(sketch, "E535", {"start": v(41.04, -7.23) * mm, "end": v(40.8, -7.23) * mm});
            skLineSegment(sketch, "E536", {"start": v(40.8, -7.23) * mm, "end": v(40.58, -7.23) * mm});
            skLineSegment(sketch, "E537", {"start": v(40.58, -7.23) * mm, "end": v(40.34, -7.23) * mm});
            skLineSegment(sketch, "E538", {"start": v(40.34, -7.23) * mm, "end": v(40.11, -7.23) * mm});
            skLineSegment(sketch, "E539", {"start": v(40.11, -7.23) * mm, "end": v(39.88, -7.23) * mm});
            skLineSegment(sketch, "E540", {"start": v(39.88, -7.23) * mm, "end": v(39.65, -7.23) * mm});
            skLineSegment(sketch, "E541", {"start": v(39.65, -7.23) * mm, "end": v(39.42, -7.23) * mm});
            skLineSegment(sketch, "E542", {"start": v(39.42, -7.23) * mm, "end": v(39.18, -7.23) * mm});
            skLineSegment(sketch, "E543", {"start": v(39.18, -7.23) * mm, "end": v(38.95, -7.23) * mm});
            skLineSegment(sketch, "E544", {"start": v(38.95, -7.23) * mm, "end": v(38.72, -7.23) * mm});
            skLineSegment(sketch, "E545", {"start": v(38.72, -7.23) * mm, "end": v(38.49, -7.23) * mm});
            skLineSegment(sketch, "E546", {"start": v(38.49, -7.23) * mm, "end": v(38.08, -6.74) * mm});
            skLineSegment(sketch, "E547", {"start": v(38.08, -6.74) * mm, "end": v(37.67, -6.24) * mm});
            skLineSegment(sketch, "E548", {"start": v(37.67, -6.24) * mm, "end": v(37.26, -5.75) * mm});
            skLineSegment(sketch, "E549", {"start": v(37.26, -5.75) * mm, "end": v(36.86, -5.25) * mm});
            skLineSegment(sketch, "E550", {"start": v(36.86, -5.25) * mm, "end": v(36.45, -4.75) * mm});
            skLineSegment(sketch, "E551", {"start": v(36.45, -4.75) * mm, "end": v(36.04, -4.26) * mm});
            skLineSegment(sketch, "E552", {"start": v(36.04, -4.26) * mm, "end": v(35.63, -3.76) * mm});
            skLineSegment(sketch, "E553", {"start": v(35.63, -3.76) * mm, "end": v(35.22, -3.27) * mm});
            skLineSegment(sketch, "E554", {"start": v(35.22, -3.27) * mm, "end": v(34.82, -2.77) * mm});
            skLineSegment(sketch, "E555", {"start": v(34.82, -2.77) * mm, "end": v(34.4, -2.27) * mm});
            skLineSegment(sketch, "E556", {"start": v(34.4, -2.27) * mm, "end": v(34, -1.78) * mm});
            skLineSegment(sketch, "E557", {"start": v(34, -1.78) * mm, "end": v(33.6, -1.28) * mm});
            skLineSegment(sketch, "E558", {"start": v(33.6, -1.28) * mm, "end": v(33.18, -0.79) * mm});
            skLineSegment(sketch, "E559", {"start": v(33.18, -0.79) * mm, "end": v(32.78, -0.29) * mm});
            skLineSegment(sketch, "E560", {"start": v(32.78, -0.29) * mm, "end": v(32.37, 0.2) * mm});
            skLineSegment(sketch, "E561", {"start": v(32.37, 0.2) * mm, "end": v(31.96, 0.7) * mm});
            skLineSegment(sketch, "E562", {"start": v(31.96, 0.7) * mm, "end": v(31.96, 0.2) * mm});
            skLineSegment(sketch, "E563", {"start": v(31.96, 0.2) * mm, "end": v(31.96, -0.29) * mm});
            skLineSegment(sketch, "E564", {"start": v(31.96, -0.29) * mm, "end": v(31.96, -0.79) * mm});
            skLineSegment(sketch, "E565", {"start": v(31.96, -0.79) * mm, "end": v(31.96, -1.28) * mm});
            skLineSegment(sketch, "E566", {"start": v(31.96, -1.28) * mm, "end": v(31.96, -1.78) * mm});
            skLineSegment(sketch, "E567", {"start": v(31.96, -1.78) * mm, "end": v(31.96, -2.27) * mm});
            skLineSegment(sketch, "E568", {"start": v(31.96, -2.27) * mm, "end": v(31.96, -2.77) * mm});
            skLineSegment(sketch, "E569", {"start": v(31.96, -2.77) * mm, "end": v(31.96, -3.27) * mm});
            skLineSegment(sketch, "E570", {"start": v(31.96, -3.27) * mm, "end": v(31.96, -3.76) * mm});
            skLineSegment(sketch, "E571", {"start": v(31.96, -3.76) * mm, "end": v(31.96, -4.26) * mm});
            skLineSegment(sketch, "E572", {"start": v(31.96, -4.26) * mm, "end": v(31.96, -4.75) * mm});
            skLineSegment(sketch, "E573", {"start": v(31.96, -4.75) * mm, "end": v(31.96, -5.25) * mm});
            skLineSegment(sketch, "E574", {"start": v(31.96, -5.25) * mm, "end": v(31.96, -5.75) * mm});
            skLineSegment(sketch, "E575", {"start": v(31.96, -5.75) * mm, "end": v(31.96, -6.24) * mm});
            skLineSegment(sketch, "E576", {"start": v(31.96, -6.24) * mm, "end": v(31.96, -6.74) * mm});
            skLineSegment(sketch, "E577", {"start": v(31.96, -6.74) * mm, "end": v(31.96, -7.23) * mm});
            skLineSegment(sketch, "E578", {"start": v(31.96, -7.23) * mm, "end": v(31.7, -7.23) * mm});
            skLineSegment(sketch, "E579", {"start": v(31.7, -7.23) * mm, "end": v(31.44, -7.23) * mm});
            skLineSegment(sketch, "E580", {"start": v(31.44, -7.23) * mm, "end": v(31.18, -7.23) * mm});
            skLineSegment(sketch, "E581", {"start": v(31.18, -7.23) * mm, "end": v(30.91, -7.23) * mm});
            skLineSegment(sketch, "E582", {"start": v(30.91, -7.23) * mm, "end": v(30.65, -7.23) * mm});
            skLineSegment(sketch, "E583", {"start": v(30.65, -7.23) * mm, "end": v(30.39, -7.23) * mm});
            skLineSegment(sketch, "E584", {"start": v(30.39, -7.23) * mm, "end": v(30.13, -7.23) * mm});
            skLineSegment(sketch, "E585", {"start": v(30.13, -7.23) * mm, "end": v(29.87, -7.23) * mm});
            skLineSegment(sketch, "E586", {"start": v(29.87, -7.23) * mm, "end": v(29.6, -7.23) * mm});
            skLineSegment(sketch, "E587", {"start": v(29.6, -7.23) * mm, "end": v(29.34, -7.23) * mm});
            skLineSegment(sketch, "E588", {"start": v(29.34, -7.23) * mm, "end": v(29.08, -7.23) * mm});
            skLineSegment(sketch, "E589", {"start": v(29.08, -7.23) * mm, "end": v(28.82, -7.23) * mm});
            skLineSegment(sketch, "E590", {"start": v(28.82, -7.23) * mm, "end": v(28.56, -7.23) * mm});
            skLineSegment(sketch, "E591", {"start": v(28.56, -7.23) * mm, "end": v(28.3, -7.23) * mm});
            skLineSegment(sketch, "E592", {"start": v(28.3, -7.23) * mm, "end": v(28.03, -7.23) * mm});
            skLineSegment(sketch, "E593", {"start": v(28.03, -7.23) * mm, "end": v(27.77, -7.23) * mm});
            skLineSegment(sketch, "E594", {"start": v(27.77, -7.23) * mm, "end": v(27.77, -6.33) * mm});
            skLineSegment(sketch, "E595", {"start": v(27.77, -6.33) * mm, "end": v(27.77, -5.43) * mm});
            skLineSegment(sketch, "E596", {"start": v(27.77, -5.43) * mm, "end": v(27.77, -4.52) * mm});
            skLineSegment(sketch, "E597", {"start": v(27.77, -4.52) * mm, "end": v(27.77, -3.62) * mm});
            skLineSegment(sketch, "E598", {"start": v(27.77, -3.62) * mm, "end": v(27.77, -2.71) * mm});
            skLineSegment(sketch, "E599", {"start": v(27.77, -2.71) * mm, "end": v(27.77, -1.8) * mm});
            skLineSegment(sketch, "E600", {"start": v(27.77, -1.8) * mm, "end": v(27.77, -0.9) * mm});
            skLineSegment(sketch, "E601", {"start": v(27.77, -0.9) * mm, "end": v(27.77, 0) * mm});
            skLineSegment(sketch, "E602", {"start": v(27.77, 0) * mm, "end": v(27.77, 0.9) * mm});
            skLineSegment(sketch, "E603", {"start": v(27.77, 0.9) * mm, "end": v(27.77, 1.8) * mm});
            skLineSegment(sketch, "E604", {"start": v(27.77, 1.8) * mm, "end": v(27.77, 2.71) * mm});
            skLineSegment(sketch, "E605", {"start": v(27.77, 2.71) * mm, "end": v(27.77, 3.62) * mm});
            skLineSegment(sketch, "E606", {"start": v(27.77, 3.62) * mm, "end": v(27.77, 4.52) * mm});
            skLineSegment(sketch, "E607", {"start": v(27.77, 4.52) * mm, "end": v(27.77, 5.43) * mm});
            skLineSegment(sketch, "E608", {"start": v(27.77, 5.43) * mm, "end": v(27.77, 6.33) * mm});
            skLineSegment(sketch, "E609", {"start": v(27.77, 6.33) * mm, "end": v(27.77, 7.23) * mm});
            skLineSegment(sketch, "E610", {"start": v(-7.87, -1.72) * mm, "end": v(-7.6, -1.72) * mm});
            skLineSegment(sketch, "E611", {"start": v(-7.6, -1.72) * mm, "end": v(-7.35, -1.72) * mm});
            skLineSegment(sketch, "E612", {"start": v(-7.35, -1.72) * mm, "end": v(-7.1, -1.72) * mm});
            skLineSegment(sketch, "E613", {"start": v(-7.1, -1.72) * mm, "end": v(-6.84, -1.72) * mm});
            skLineSegment(sketch, "E614", {"start": v(-6.84, -1.72) * mm, "end": v(-6.59, -1.72) * mm});
            skLineSegment(sketch, "E615", {"start": v(-6.59, -1.72) * mm, "end": v(-6.33, -1.72) * mm});
            skLineSegment(sketch, "E616", {"start": v(-6.33, -1.72) * mm, "end": v(-6.07, -1.72) * mm});
            skLineSegment(sketch, "E617", {"start": v(-6.07, -1.72) * mm, "end": v(-5.82, -1.72) * mm});
            skLineSegment(sketch, "E618", {"start": v(-5.82, -1.72) * mm, "end": v(-5.56, -1.72) * mm});
            skLineSegment(sketch, "E619", {"start": v(-5.56, -1.72) * mm, "end": v(-5.3, -1.72) * mm});
            skLineSegment(sketch, "E620", {"start": v(-5.3, -1.72) * mm, "end": v(-5.05, -1.72) * mm});
            skLineSegment(sketch, "E621", {"start": v(-5.05, -1.72) * mm, "end": v(-4.8, -1.72) * mm});
            skLineSegment(sketch, "E622", {"start": v(-4.8, -1.72) * mm, "end": v(-4.54, -1.72) * mm});
            skLineSegment(sketch, "E623", {"start": v(-4.54, -1.72) * mm, "end": v(-4.28, -1.72) * mm});
            skLineSegment(sketch, "E624", {"start": v(-4.28, -1.72) * mm, "end": v(-4.03, -1.72) * mm});
            skLineSegment(sketch, "E625", {"start": v(-4.03, -1.72) * mm, "end": v(-3.77, -1.72) * mm});
            skLineSegment(sketch, "E626", {"start": v(-3.77, -1.72) * mm, "end": v(-3.77, -1.83) * mm});
            skLineSegment(sketch, "E627", {"start": v(-3.77, -1.83) * mm, "end": v(-3.77, -1.94) * mm});
            skLineSegment(sketch, "E628", {"start": v(-3.77, -1.94) * mm, "end": v(-3.77, -2.04) * mm});
            skLineSegment(sketch, "E629", {"start": v(-3.77, -2.04) * mm, "end": v(-3.77, -2.15) * mm});
            skLineSegment(sketch, "E630", {"start": v(-3.77, -2.15) * mm, "end": v(-3.77, -2.26) * mm});
            skLineSegment(sketch, "E631", {"start": v(-3.77, -2.26) * mm, "end": v(-3.77, -2.37) * mm});
            skLineSegment(sketch, "E632", {"start": v(-3.77, -2.37) * mm, "end": v(-3.77, -2.48) * mm});
            skLineSegment(sketch, "E633", {"start": v(-3.77, -2.48) * mm, "end": v(-3.77, -2.6) * mm});
            skLineSegment(sketch, "E634", {"start": v(-3.77, -2.6) * mm, "end": v(-3.77, -2.7) * mm});
            skLineSegment(sketch, "E635", {"start": v(-3.77, -2.7) * mm, "end": v(-3.77, -2.81) * mm});
            skLineSegment(sketch, "E636", {"start": v(-3.77, -2.81) * mm, "end": v(-3.77, -2.92) * mm});
            skLineSegment(sketch, "E637", {"start": v(-3.77, -2.92) * mm, "end": v(-3.77, -3.03) * mm});
            skLineSegment(sketch, "E638", {"start": v(-3.77, -3.03) * mm, "end": v(-3.77, -3.14) * mm});
            skLineSegment(sketch, "E639", {"start": v(-3.77, -3.14) * mm, "end": v(-3.77, -3.25) * mm});
            skLineSegment(sketch, "E640", {"start": v(-3.77, -3.25) * mm, "end": v(-3.77, -3.36) * mm});
            skLineSegment(sketch, "E641", {"start": v(-3.77, -3.36) * mm, "end": v(-3.77, -3.47) * mm});
            skLineSegment(sketch, "E642", {"start": v(-3.77, -3.47) * mm, "end": v(-3.9, -3.54) * mm});
            skLineSegment(sketch, "E643", {"start": v(-3.9, -3.54) * mm, "end": v(-4.01, -3.61) * mm});
            skLineSegment(sketch, "E644", {"start": v(-4.01, -3.61) * mm, "end": v(-4.14, -3.67) * mm});
            skLineSegment(sketch, "E645", {"start": v(-4.14, -3.67) * mm, "end": v(-4.27, -3.73) * mm});
            skLineSegment(sketch, "E646", {"start": v(-4.27, -3.73) * mm, "end": v(-4.41, -3.79) * mm});
            skLineSegment(sketch, "E647", {"start": v(-4.41, -3.79) * mm, "end": v(-4.55, -3.84) * mm});
            skLineSegment(sketch, "E648", {"start": v(-4.55, -3.84) * mm, "end": v(-4.7, -3.88) * mm});
            skLineSegment(sketch, "E649", {"start": v(-4.7, -3.88) * mm, "end": v(-4.84, -3.92) * mm});
            skLineSegment(sketch, "E650", {"start": v(-4.84, -3.92) * mm, "end": v(-5, -3.95) * mm});
            skLineSegment(sketch, "E651", {"start": v(-5, -3.95) * mm, "end": v(-5.16, -3.99) * mm});
            skLineSegment(sketch, "E652", {"start": v(-5.16, -3.99) * mm, "end": v(-5.32, -4.01) * mm});
            skLineSegment(sketch, "E653", {"start": v(-5.32, -4.01) * mm, "end": v(-5.49, -4.03) * mm});
            skLineSegment(sketch, "E654", {"start": v(-5.49, -4.03) * mm, "end": v(-5.66, -4.05) * mm});
            skLineSegment(sketch, "E655", {"start": v(-5.66, -4.05) * mm, "end": v(-5.84, -4.06) * mm});
            skLineSegment(sketch, "E656", {"start": v(-5.84, -4.06) * mm, "end": v(-6.03, -4.07) * mm});
            skLineSegment(sketch, "E657", {"start": v(-6.03, -4.07) * mm, "end": v(-6.22, -4.07) * mm});
            skLineSegment(sketch, "E658", {"start": v(-6.22, -4.07) * mm, "end": v(-6.66, -4.05) * mm});
            skLineSegment(sketch, "E659", {"start": v(-6.66, -4.05) * mm, "end": v(-7.09, -4) * mm});
            skLineSegment(sketch, "E660", {"start": v(-7.09, -4) * mm, "end": v(-7.5, -3.9) * mm});
            skLineSegment(sketch, "E661", {"start": v(-7.5, -3.9) * mm, "end": v(-7.89, -3.77) * mm});
            skLineSegment(sketch, "E662", {"start": v(-7.89, -3.77) * mm, "end": v(-8.25, -3.61) * mm});
            skLineSegment(sketch, "E663", {"start": v(-8.25, -3.61) * mm, "end": v(-8.6, -3.42) * mm});
            skLineSegment(sketch, "E664", {"start": v(-8.6, -3.42) * mm, "end": v(-8.9, -3.2) * mm});
            skLineSegment(sketch, "E665", {"start": v(-8.9, -3.2) * mm, "end": v(-9.2, -2.94) * mm});
            skLineSegment(sketch, "E666", {"start": v(-9.2, -2.94) * mm, "end": v(-9.46, -2.66) * mm});
            skLineSegment(sketch, "E667", {"start": v(-9.46, -2.66) * mm, "end": v(-9.69, -2.36) * mm});
            skLineSegment(sketch, "E668", {"start": v(-9.69, -2.36) * mm, "end": v(-9.89, -2.03) * mm});
            skLineSegment(sketch, "E669", {"start": v(-9.89, -2.03) * mm, "end": v(-10.06, -1.67) * mm});
            skLineSegment(sketch, "E670", {"start": v(-10.06, -1.67) * mm, "end": v(-10.19, -1.3) * mm});
            skLineSegment(sketch, "E671", {"start": v(-10.19, -1.3) * mm, "end": v(-10.28, -0.9) * mm});
            skLineSegment(sketch, "E672", {"start": v(-10.28, -0.9) * mm, "end": v(-10.34, -0.5) * mm});
            skLineSegment(sketch, "E673", {"start": v(-10.34, -0.5) * mm, "end": v(-10.36, -0.06) * mm});
            skLineSegment(sketch, "E674", {"start": v(-10.36, -0.06) * mm, "end": v(-10.36, -0.06) * mm});
            skLineSegment(sketch, "E675", {"start": v(-10.36, -0.06) * mm, "end": v(-10.36, -0.05) * mm});
            skLineSegment(sketch, "E676", {"start": v(-10.36, -0.05) * mm, "end": v(-10.36, -0.05) * mm});
            skLineSegment(sketch, "E677", {"start": v(-10.36, -0.05) * mm, "end": v(-10.36, -0.04) * mm});
            skLineSegment(sketch, "E678", {"start": v(-10.36, -0.04) * mm, "end": v(-10.36, -0.04) * mm});
            skLineSegment(sketch, "E679", {"start": v(-10.36, -0.04) * mm, "end": v(-10.36, -0.03) * mm});
            skLineSegment(sketch, "E680", {"start": v(-10.36, -0.03) * mm, "end": v(-10.36, -0.03) * mm});
            skLineSegment(sketch, "E681", {"start": v(-10.36, -0.03) * mm, "end": v(-10.36, -0.02) * mm});
            skLineSegment(sketch, "E682", {"start": v(-10.36, -0.02) * mm, "end": v(-10.36, -0.02) * mm});
            skLineSegment(sketch, "E683", {"start": v(-10.36, -0.02) * mm, "end": v(-10.34, 0.39) * mm});
            skLineSegment(sketch, "E684", {"start": v(-10.34, 0.39) * mm, "end": v(-10.29, 0.78) * mm});
            skLineSegment(sketch, "E685", {"start": v(-10.29, 0.78) * mm, "end": v(-10.2, 1.17) * mm});
            skLineSegment(sketch, "E686", {"start": v(-10.2, 1.17) * mm, "end": v(-10.06, 1.53) * mm});
            skLineSegment(sketch, "E687", {"start": v(-10.06, 1.53) * mm, "end": v(-9.9, 1.88) * mm});
            skLineSegment(sketch, "E688", {"start": v(-9.9, 1.88) * mm, "end": v(-9.7, 2.2) * mm});
            skLineSegment(sketch, "E689", {"start": v(-9.7, 2.2) * mm, "end": v(-9.49, 2.51) * mm});
            skLineSegment(sketch, "E690", {"start": v(-9.49, 2.51) * mm, "end": v(-9.24, 2.8) * mm});
            skLineSegment(sketch, "E691", {"start": v(-9.24, 2.8) * mm, "end": v(-8.96, 3.05) * mm});
            skLineSegment(sketch, "E692", {"start": v(-8.96, 3.05) * mm, "end": v(-8.66, 3.28) * mm});
            skLineSegment(sketch, "E693", {"start": v(-8.66, 3.28) * mm, "end": v(-8.34, 3.47) * mm});
            skLineSegment(sketch, "E694", {"start": v(-8.34, 3.47) * mm, "end": v(-8, 3.64) * mm});
            skLineSegment(sketch, "E695", {"start": v(-8, 3.64) * mm, "end": v(-7.64, 3.77) * mm});
            skLineSegment(sketch, "E696", {"start": v(-7.64, 3.77) * mm, "end": v(-7.26, 3.87) * mm});
            skLineSegment(sketch, "E697", {"start": v(-7.26, 3.87) * mm, "end": v(-6.86, 3.93) * mm});
            skLineSegment(sketch, "E698", {"start": v(-6.86, 3.93) * mm, "end": v(-6.46, 3.95) * mm});
            skLineSegment(sketch, "E699", {"start": v(-6.46, 3.95) * mm, "end": v(-6.26, 3.95) * mm});
            skLineSegment(sketch, "E700", {"start": v(-6.26, 3.95) * mm, "end": v(-6.06, 3.94) * mm});
            skLineSegment(sketch, "E701", {"start": v(-6.06, 3.94) * mm, "end": v(-5.88, 3.92) * mm});
            skLineSegment(sketch, "E702", {"start": v(-5.88, 3.92) * mm, "end": v(-5.7, 3.9) * mm});
            skLineSegment(sketch, "E703", {"start": v(-5.7, 3.9) * mm, "end": v(-5.5, 3.88) * mm});
            skLineSegment(sketch, "E704", {"start": v(-5.5, 3.88) * mm, "end": v(-5.33, 3.84) * mm});
            skLineSegment(sketch, "E705", {"start": v(-5.33, 3.84) * mm, "end": v(-5.16, 3.8) * mm});
            skLineSegment(sketch, "E706", {"start": v(-5.16, 3.8) * mm, "end": v(-4.99, 3.76) * mm});
            skLineSegment(sketch, "E707", {"start": v(-4.99, 3.76) * mm, "end": v(-4.82, 3.72) * mm});
            skLineSegment(sketch, "E708", {"start": v(-4.82, 3.72) * mm, "end": v(-4.66, 3.66) * mm});
            skLineSegment(sketch, "E709", {"start": v(-4.66, 3.66) * mm, "end": v(-4.5, 3.6) * mm});
            skLineSegment(sketch, "E710", {"start": v(-4.5, 3.6) * mm, "end": v(-4.34, 3.54) * mm});
            skLineSegment(sketch, "E711", {"start": v(-4.34, 3.54) * mm, "end": v(-4.18, 3.47) * mm});
            skLineSegment(sketch, "E712", {"start": v(-4.18, 3.47) * mm, "end": v(-4.03, 3.4) * mm});
            skLineSegment(sketch, "E713", {"start": v(-4.03, 3.4) * mm, "end": v(-3.88, 3.32) * mm});
            skLineSegment(sketch, "E714", {"start": v(-3.88, 3.32) * mm, "end": v(-3.72, 3.24) * mm});
            skLineSegment(sketch, "E715", {"start": v(-3.72, 3.24) * mm, "end": v(-3.54, 3.4) * mm});
            skLineSegment(sketch, "E716", {"start": v(-3.54, 3.4) * mm, "end": v(-3.35, 3.55) * mm});
            skLineSegment(sketch, "E717", {"start": v(-3.35, 3.55) * mm, "end": v(-3.16, 3.7) * mm});
            skLineSegment(sketch, "E718", {"start": v(-3.16, 3.7) * mm, "end": v(-2.98, 3.87) * mm});
            skLineSegment(sketch, "E719", {"start": v(-2.98, 3.87) * mm, "end": v(-2.79, 4.02) * mm});
            skLineSegment(sketch, "E720", {"start": v(-2.79, 4.02) * mm, "end": v(-2.6, 4.18) * mm});
            skLineSegment(sketch, "E721", {"start": v(-2.6, 4.18) * mm, "end": v(-2.41, 4.34) * mm});
            skLineSegment(sketch, "E722", {"start": v(-2.41, 4.34) * mm, "end": v(-2.23, 4.5) * mm});
            skLineSegment(sketch, "E723", {"start": v(-2.23, 4.5) * mm, "end": v(-2.04, 4.66) * mm});
            skLineSegment(sketch, "E724", {"start": v(-2.04, 4.66) * mm, "end": v(-1.85, 4.81) * mm});
            skLineSegment(sketch, "E725", {"start": v(-1.85, 4.81) * mm, "end": v(-1.67, 4.97) * mm});
            skLineSegment(sketch, "E726", {"start": v(-1.67, 4.97) * mm, "end": v(-1.48, 5.13) * mm});
            skLineSegment(sketch, "E727", {"start": v(-1.48, 5.13) * mm, "end": v(-1.3, 5.29) * mm});
            skLineSegment(sketch, "E728", {"start": v(-1.3, 5.29) * mm, "end": v(-1.1, 5.44) * mm});
            skLineSegment(sketch, "E729", {"start": v(-1.1, 5.44) * mm, "end": v(-0.92, 5.6) * mm});
            skLineSegment(sketch, "E730", {"start": v(-0.92, 5.6) * mm, "end": v(-0.73, 5.76) * mm});
            skLineSegment(sketch, "E731", {"start": v(-0.73, 5.76) * mm, "end": v(-1.02, 5.96) * mm});
            skLineSegment(sketch, "E732", {"start": v(-1.02, 5.96) * mm, "end": v(-1.31, 6.15) * mm});
            skLineSegment(sketch, "E733", {"start": v(-1.31, 6.15) * mm, "end": v(-1.62, 6.33) * mm});
            skLineSegment(sketch, "E734", {"start": v(-1.62, 6.33) * mm, "end": v(-1.93, 6.5) * mm});
            skLineSegment(sketch, "E735", {"start": v(-1.93, 6.5) * mm, "end": v(-2.25, 6.66) * mm});
            skLineSegment(sketch, "E736", {"start": v(-2.25, 6.66) * mm, "end": v(-2.57, 6.8) * mm});
            skLineSegment(sketch, "E737", {"start": v(-2.57, 6.8) * mm, "end": v(-2.91, 6.94) * mm});
            skLineSegment(sketch, "E738", {"start": v(-2.91, 6.94) * mm, "end": v(-3.26, 7.06) * mm});
            skLineSegment(sketch, "E739", {"start": v(-3.26, 7.06) * mm, "end": v(-3.62, 7.17) * mm});
            skLineSegment(sketch, "E740", {"start": v(-3.62, 7.17) * mm, "end": v(-3.99, 7.26) * mm});
            skLineSegment(sketch, "E741", {"start": v(-3.99, 7.26) * mm, "end": v(-4.37, 7.34) * mm});
            skLineSegment(sketch, "E742", {"start": v(-4.37, 7.34) * mm, "end": v(-4.76, 7.4) * mm});
            skLineSegment(sketch, "E743", {"start": v(-4.76, 7.4) * mm, "end": v(-5.17, 7.46) * mm});
            skLineSegment(sketch, "E744", {"start": v(-5.17, 7.46) * mm, "end": v(-5.6, 7.5) * mm});
            skLineSegment(sketch, "E745", {"start": v(-5.6, 7.5) * mm, "end": v(-6.03, 7.52) * mm});
            skLineSegment(sketch, "E746", {"start": v(-6.03, 7.52) * mm, "end": v(-6.48, 7.52) * mm});
            skLineSegment(sketch, "E747", {"start": v(-6.48, 7.52) * mm, "end": v(-7.35, 7.49) * mm});
            skLineSegment(sketch, "E748", {"start": v(-7.35, 7.49) * mm, "end": v(-8.2, 7.37) * mm});
            skLineSegment(sketch, "E749", {"start": v(-8.2, 7.37) * mm, "end": v(-9, 7.2) * mm});
            skLineSegment(sketch, "E750", {"start": v(-9, 7.2) * mm, "end": v(-9.76, 6.94) * mm});
            skLineSegment(sketch, "E751", {"start": v(-9.76, 6.94) * mm, "end": v(-10.49, 6.63) * mm});
            skLineSegment(sketch, "E752", {"start": v(-10.49, 6.63) * mm, "end": v(-11.16, 6.25) * mm});
            skLineSegment(sketch, "E753", {"start": v(-11.16, 6.25) * mm, "end": v(-11.8, 5.83) * mm});
            skLineSegment(sketch, "E754", {"start": v(-11.8, 5.83) * mm, "end": v(-12.37, 5.34) * mm});
            skLineSegment(sketch, "E755", {"start": v(-12.37, 5.34) * mm, "end": v(-12.9, 4.81) * mm});
            skLineSegment(sketch, "E756", {"start": v(-12.9, 4.81) * mm, "end": v(-13.35, 4.23) * mm});
            skLineSegment(sketch, "E757", {"start": v(-13.35, 4.23) * mm, "end": v(-13.75, 3.61) * mm});
            skLineSegment(sketch, "E758", {"start": v(-13.75, 3.61) * mm, "end": v(-14.09, 2.95) * mm});
            skLineSegment(sketch, "E759", {"start": v(-14.09, 2.95) * mm, "end": v(-14.35, 2.26) * mm});
            skLineSegment(sketch, "E760", {"start": v(-14.35, 2.26) * mm, "end": v(-14.55, 1.53) * mm});
            skLineSegment(sketch, "E761", {"start": v(-14.55, 1.53) * mm, "end": v(-14.67, 0.78) * mm});
            skLineSegment(sketch, "E762", {"start": v(-14.67, 0.78) * mm, "end": v(-14.7, 0) * mm});
            skLineSegment(sketch, "E763", {"start": v(-14.7, 0) * mm, "end": v(-14.7, 0) * mm});
            skLineSegment(sketch, "E764", {"start": v(-14.7, 0) * mm, "end": v(-14.7, -0.01) * mm});
            skLineSegment(sketch, "E765", {"start": v(-14.7, -0.01) * mm, "end": v(-14.7, -0.01) * mm});
            skLineSegment(sketch, "E766", {"start": v(-14.7, -0.01) * mm, "end": v(-14.7, -0.02) * mm});
            skLineSegment(sketch, "E767", {"start": v(-14.7, -0.02) * mm, "end": v(-14.7, -0.02) * mm});
            skLineSegment(sketch, "E768", {"start": v(-14.7, -0.02) * mm, "end": v(-14.7, -0.03) * mm});
            skLineSegment(sketch, "E769", {"start": v(-14.7, -0.03) * mm, "end": v(-14.7, -0.03) * mm});
            skLineSegment(sketch, "E770", {"start": v(-14.7, -0.03) * mm, "end": v(-14.7, -0.04) * mm});
            skLineSegment(sketch, "E771", {"start": v(-14.7, -0.04) * mm, "end": v(-14.7, -0.04) * mm});
            skLineSegment(sketch, "E772", {"start": v(-14.7, -0.04) * mm, "end": v(-14.67, -0.85) * mm});
            skLineSegment(sketch, "E773", {"start": v(-14.67, -0.85) * mm, "end": v(-14.54, -1.62) * mm});
            skLineSegment(sketch, "E774", {"start": v(-14.54, -1.62) * mm, "end": v(-14.35, -2.36) * mm});
            skLineSegment(sketch, "E775", {"start": v(-14.35, -2.36) * mm, "end": v(-14.08, -3.06) * mm});
            skLineSegment(sketch, "E776", {"start": v(-14.08, -3.06) * mm, "end": v(-13.74, -3.72) * mm});
            skLineSegment(sketch, "E777", {"start": v(-13.74, -3.72) * mm, "end": v(-13.33, -4.33) * mm});
            skLineSegment(sketch, "E778", {"start": v(-13.33, -4.33) * mm, "end": v(-12.86, -4.9) * mm});
            skLineSegment(sketch, "E779", {"start": v(-12.86, -4.9) * mm, "end": v(-12.33, -5.43) * mm});
            skLineSegment(sketch, "E780", {"start": v(-12.33, -5.43) * mm, "end": v(-11.75, -5.9) * mm});
            skLineSegment(sketch, "E781", {"start": v(-11.75, -5.9) * mm, "end": v(-11.11, -6.31) * mm});
            skLineSegment(sketch, "E782", {"start": v(-11.11, -6.31) * mm, "end": v(-10.43, -6.67) * mm});
            skLineSegment(sketch, "E783", {"start": v(-10.43, -6.67) * mm, "end": v(-9.7, -6.97) * mm});
            skLineSegment(sketch, "E784", {"start": v(-9.7, -6.97) * mm, "end": v(-8.92, -7.2) * mm});
            skLineSegment(sketch, "E785", {"start": v(-8.92, -7.2) * mm, "end": v(-8.11, -7.38) * mm});
            skLineSegment(sketch, "E786", {"start": v(-8.11, -7.38) * mm, "end": v(-7.27, -7.49) * mm});
            skLineSegment(sketch, "E787", {"start": v(-7.27, -7.49) * mm, "end": v(-6.39, -7.52) * mm});
            skLineSegment(sketch, "E788", {"start": v(-6.39, -7.52) * mm, "end": v(-5.88, -7.51) * mm});
            skLineSegment(sketch, "E789", {"start": v(-5.88, -7.51) * mm, "end": v(-5.37, -7.48) * mm});
            skLineSegment(sketch, "E790", {"start": v(-5.37, -7.48) * mm, "end": v(-4.89, -7.43) * mm});
            skLineSegment(sketch, "E791", {"start": v(-4.89, -7.43) * mm, "end": v(-4.41, -7.35) * mm});
            skLineSegment(sketch, "E792", {"start": v(-4.41, -7.35) * mm, "end": v(-3.95, -7.26) * mm});
            skLineSegment(sketch, "E793", {"start": v(-3.95, -7.26) * mm, "end": v(-3.5, -7.15) * mm});
            skLineSegment(sketch, "E794", {"start": v(-3.5, -7.15) * mm, "end": v(-3.06, -7.02) * mm});
            skLineSegment(sketch, "E795", {"start": v(-3.06, -7.02) * mm, "end": v(-2.64, -6.88) * mm});
            skLineSegment(sketch, "E796", {"start": v(-2.64, -6.88) * mm, "end": v(-2.23, -6.72) * mm});
            skLineSegment(sketch, "E797", {"start": v(-2.23, -6.72) * mm, "end": v(-1.83, -6.55) * mm});
            skLineSegment(sketch, "E798", {"start": v(-1.83, -6.55) * mm, "end": v(-1.45, -6.37) * mm});
            skLineSegment(sketch, "E799", {"start": v(-1.45, -6.37) * mm, "end": v(-1.08, -6.17) * mm});
            skLineSegment(sketch, "E800", {"start": v(-1.08, -6.17) * mm, "end": v(-0.73, -5.97) * mm});
            skLineSegment(sketch, "E801", {"start": v(-0.73, -5.97) * mm, "end": v(-0.39, -5.75) * mm});
            skLineSegment(sketch, "E802", {"start": v(-0.39, -5.75) * mm, "end": v(-0.06, -5.52) * mm});
            skLineSegment(sketch, "E803", {"start": v(-0.06, -5.52) * mm, "end": v(0.25, -5.3) * mm});
            skLineSegment(sketch, "E804", {"start": v(0.25, -5.3) * mm, "end": v(0.25, -4.88) * mm});
            skLineSegment(sketch, "E805", {"start": v(0.25, -4.88) * mm, "end": v(0.25, -4.48) * mm});
            skLineSegment(sketch, "E806", {"start": v(0.25, -4.48) * mm, "end": v(0.25, -4.07) * mm});
            skLineSegment(sketch, "E807", {"start": v(0.25, -4.07) * mm, "end": v(0.25, -3.66) * mm});
            skLineSegment(sketch, "E808", {"start": v(0.25, -3.66) * mm, "end": v(0.25, -3.26) * mm});
            skLineSegment(sketch, "E809", {"start": v(0.25, -3.26) * mm, "end": v(0.25, -2.85) * mm});
            skLineSegment(sketch, "E810", {"start": v(0.25, -2.85) * mm, "end": v(0.25, -2.44) * mm});
            skLineSegment(sketch, "E811", {"start": v(0.25, -2.44) * mm, "end": v(0.25, -2.04) * mm});
            skLineSegment(sketch, "E812", {"start": v(0.25, -2.04) * mm, "end": v(0.25, -1.63) * mm});
            skLineSegment(sketch, "E813", {"start": v(0.25, -1.63) * mm, "end": v(0.25, -1.22) * mm});
            skLineSegment(sketch, "E814", {"start": v(0.25, -1.22) * mm, "end": v(0.25, -0.81) * mm});
            skLineSegment(sketch, "E815", {"start": v(0.25, -0.81) * mm, "end": v(0.25, -0.4) * mm});
            skLineSegment(sketch, "E816", {"start": v(0.25, -0.4) * mm, "end": v(0.25, 0) * mm});
            skLineSegment(sketch, "E817", {"start": v(0.25, 0) * mm, "end": v(0.25, 0.4) * mm});
            skLineSegment(sketch, "E818", {"start": v(0.25, 0.4) * mm, "end": v(0.25, 0.81) * mm});
            skLineSegment(sketch, "E819", {"start": v(0.25, 0.81) * mm, "end": v(0.25, 1.22) * mm});
            skLineSegment(sketch, "E820", {"start": v(0.25, 1.22) * mm, "end": v(-0.04, 1.22) * mm});
            skLineSegment(sketch, "E821", {"start": v(-0.04, 1.22) * mm, "end": v(-0.33, 1.22) * mm});
            skLineSegment(sketch, "E822", {"start": v(-0.33, 1.22) * mm, "end": v(-0.62, 1.22) * mm});
            skLineSegment(sketch, "E823", {"start": v(-0.62, 1.22) * mm, "end": v(-0.91, 1.22) * mm});
            skLineSegment(sketch, "E824", {"start": v(-0.91, 1.22) * mm, "end": v(-1.2, 1.22) * mm});
            skLineSegment(sketch, "E825", {"start": v(-1.2, 1.22) * mm, "end": v(-1.5, 1.22) * mm});
            skLineSegment(sketch, "E826", {"start": v(-1.5, 1.22) * mm, "end": v(-1.78, 1.22) * mm});
            skLineSegment(sketch, "E827", {"start": v(-1.78, 1.22) * mm, "end": v(-2.07, 1.22) * mm});
            skLineSegment(sketch, "E828", {"start": v(-2.07, 1.22) * mm, "end": v(-2.36, 1.22) * mm});
            skLineSegment(sketch, "E829", {"start": v(-2.36, 1.22) * mm, "end": v(-2.65, 1.22) * mm});
            skLineSegment(sketch, "E830", {"start": v(-2.65, 1.22) * mm, "end": v(-2.95, 1.22) * mm});
            skLineSegment(sketch, "E831", {"start": v(-2.95, 1.22) * mm, "end": v(-3.24, 1.22) * mm});
            skLineSegment(sketch, "E832", {"start": v(-3.24, 1.22) * mm, "end": v(-3.53, 1.22) * mm});
            skLineSegment(sketch, "E833", {"start": v(-3.53, 1.22) * mm, "end": v(-3.82, 1.22) * mm});
            skLineSegment(sketch, "E834", {"start": v(-3.82, 1.22) * mm, "end": v(-4.1, 1.22) * mm});
            skLineSegment(sketch, "E835", {"start": v(-4.1, 1.22) * mm, "end": v(-4.4, 1.22) * mm});
            skLineSegment(sketch, "E836", {"start": v(-4.4, 1.22) * mm, "end": v(-4.61, 1.04) * mm});
            skLineSegment(sketch, "E837", {"start": v(-4.61, 1.04) * mm, "end": v(-4.83, 0.85) * mm});
            skLineSegment(sketch, "E838", {"start": v(-4.83, 0.85) * mm, "end": v(-5.05, 0.67) * mm});
            skLineSegment(sketch, "E839", {"start": v(-5.05, 0.67) * mm, "end": v(-5.26, 0.49) * mm});
            skLineSegment(sketch, "E840", {"start": v(-5.26, 0.49) * mm, "end": v(-5.48, 0.3) * mm});
            skLineSegment(sketch, "E841", {"start": v(-5.48, 0.3) * mm, "end": v(-5.7, 0.12) * mm});
            skLineSegment(sketch, "E842", {"start": v(-5.7, 0.12) * mm, "end": v(-5.91, -0.06) * mm});
            skLineSegment(sketch, "E843", {"start": v(-5.91, -0.06) * mm, "end": v(-6.13, -0.25) * mm});
            skLineSegment(sketch, "E844", {"start": v(-6.13, -0.25) * mm, "end": v(-6.35, -0.43) * mm});
            skLineSegment(sketch, "E845", {"start": v(-6.35, -0.43) * mm, "end": v(-6.56, -0.61) * mm});
            skLineSegment(sketch, "E846", {"start": v(-6.56, -0.61) * mm, "end": v(-6.78, -0.8) * mm});
            skLineSegment(sketch, "E847", {"start": v(-6.78, -0.8) * mm, "end": v(-7, -0.98) * mm});
            skLineSegment(sketch, "E848", {"start": v(-7, -0.98) * mm, "end": v(-7.22, -1.16) * mm});
            skLineSegment(sketch, "E849", {"start": v(-7.22, -1.16) * mm, "end": v(-7.43, -1.35) * mm});
            skLineSegment(sketch, "E850", {"start": v(-7.43, -1.35) * mm, "end": v(-7.65, -1.53) * mm});
            skLineSegment(sketch, "E851", {"start": v(-7.65, -1.53) * mm, "end": v(-7.87, -1.72) * mm});
            skLineSegment(sketch, "E852", {"start": v(6.83, 7.22) * mm, "end": v(6.57, 7) * mm});
            skLineSegment(sketch, "E853", {"start": v(6.57, 7) * mm, "end": v(6.3, 6.77) * mm});
            skLineSegment(sketch, "E854", {"start": v(6.3, 6.77) * mm, "end": v(6.03, 6.55) * mm});
            skLineSegment(sketch, "E855", {"start": v(6.03, 6.55) * mm, "end": v(5.77, 6.32) * mm});
            skLineSegment(sketch, "E856", {"start": v(5.77, 6.32) * mm, "end": v(5.5, 6.1) * mm});
            skLineSegment(sketch, "E857", {"start": v(5.5, 6.1) * mm, "end": v(5.24, 5.87) * mm});
            skLineSegment(sketch, "E858", {"start": v(5.24, 5.87) * mm, "end": v(4.97, 5.65) * mm});
            skLineSegment(sketch, "E859", {"start": v(4.97, 5.65) * mm, "end": v(4.7, 5.42) * mm});
            skLineSegment(sketch, "E860", {"start": v(4.7, 5.42) * mm, "end": v(4.44, 5.2) * mm});
            skLineSegment(sketch, "E861", {"start": v(4.44, 5.2) * mm, "end": v(4.17, 4.97) * mm});
            skLineSegment(sketch, "E862", {"start": v(4.17, 4.97) * mm, "end": v(3.9, 4.75) * mm});
            skLineSegment(sketch, "E863", {"start": v(3.9, 4.75) * mm, "end": v(3.64, 4.52) * mm});
            skLineSegment(sketch, "E864", {"start": v(3.64, 4.52) * mm, "end": v(3.37, 4.3) * mm});
            skLineSegment(sketch, "E865", {"start": v(3.37, 4.3) * mm, "end": v(3.1, 4.08) * mm});
            skLineSegment(sketch, "E866", {"start": v(3.1, 4.08) * mm, "end": v(2.84, 3.85) * mm});
            skLineSegment(sketch, "E867", {"start": v(2.84, 3.85) * mm, "end": v(2.58, 3.63) * mm});
            skLineSegment(sketch, "E868", {"start": v(2.58, 3.63) * mm, "end": v(2.58, 2.95) * mm});
            skLineSegment(sketch, "E869", {"start": v(2.58, 2.95) * mm, "end": v(2.58, 2.27) * mm});
            skLineSegment(sketch, "E870", {"start": v(2.58, 2.27) * mm, "end": v(2.58, 1.59) * mm});
            skLineSegment(sketch, "E871", {"start": v(2.58, 1.59) * mm, "end": v(2.58, 0.91) * mm});
            skLineSegment(sketch, "E872", {"start": v(2.58, 0.91) * mm, "end": v(2.58, 0.23) * mm});
            skLineSegment(sketch, "E873", {"start": v(2.58, 0.23) * mm, "end": v(2.58, -0.45) * mm});
            skLineSegment(sketch, "E874", {"start": v(2.58, -0.45) * mm, "end": v(2.58, -1.13) * mm});
            skLineSegment(sketch, "E875", {"start": v(2.58, -1.13) * mm, "end": v(2.58, -1.8) * mm});
            skLineSegment(sketch, "E876", {"start": v(2.58, -1.8) * mm, "end": v(2.58, -2.48) * mm});
            skLineSegment(sketch, "E877", {"start": v(2.58, -2.48) * mm, "end": v(2.58, -3.16) * mm});
            skLineSegment(sketch, "E878", {"start": v(2.58, -3.16) * mm, "end": v(2.58, -3.84) * mm});
            skLineSegment(sketch, "E879", {"start": v(2.58, -3.84) * mm, "end": v(2.58, -4.52) * mm});
            skLineSegment(sketch, "E880", {"start": v(2.58, -4.52) * mm, "end": v(2.58, -5.2) * mm});
            skLineSegment(sketch, "E881", {"start": v(2.58, -5.2) * mm, "end": v(2.58, -5.88) * mm});
            skLineSegment(sketch, "E882", {"start": v(2.58, -5.88) * mm, "end": v(2.58, -6.56) * mm});
            skLineSegment(sketch, "E883", {"start": v(2.58, -6.56) * mm, "end": v(2.58, -7.23) * mm});
            skLineSegment(sketch, "E884", {"start": v(2.58, -7.23) * mm, "end": v(2.84, -7.23) * mm});
            skLineSegment(sketch, "E885", {"start": v(2.84, -7.23) * mm, "end": v(3.1, -7.23) * mm});
            skLineSegment(sketch, "E886", {"start": v(3.1, -7.23) * mm, "end": v(3.37, -7.23) * mm});
            skLineSegment(sketch, "E887", {"start": v(3.37, -7.23) * mm, "end": v(3.64, -7.23) * mm});
            skLineSegment(sketch, "E888", {"start": v(3.64, -7.23) * mm, "end": v(3.9, -7.23) * mm});
            skLineSegment(sketch, "E889", {"start": v(3.9, -7.23) * mm, "end": v(4.17, -7.23) * mm});
            skLineSegment(sketch, "E890", {"start": v(4.17, -7.23) * mm, "end": v(4.44, -7.23) * mm});
            skLineSegment(sketch, "E891", {"start": v(4.44, -7.23) * mm, "end": v(4.7, -7.23) * mm});
            skLineSegment(sketch, "E892", {"start": v(4.7, -7.23) * mm, "end": v(4.97, -7.23) * mm});
            skLineSegment(sketch, "E893", {"start": v(4.97, -7.23) * mm, "end": v(5.24, -7.23) * mm});
            skLineSegment(sketch, "E894", {"start": v(5.24, -7.23) * mm, "end": v(5.5, -7.23) * mm});
            skLineSegment(sketch, "E895", {"start": v(5.5, -7.23) * mm, "end": v(5.77, -7.23) * mm});
            skLineSegment(sketch, "E896", {"start": v(5.77, -7.23) * mm, "end": v(6.03, -7.23) * mm});
            skLineSegment(sketch, "E897", {"start": v(6.03, -7.23) * mm, "end": v(6.3, -7.23) * mm});
            skLineSegment(sketch, "E898", {"start": v(6.3, -7.23) * mm, "end": v(6.57, -7.23) * mm});
            skLineSegment(sketch, "E899", {"start": v(6.57, -7.23) * mm, "end": v(6.83, -7.23) * mm});
            skLineSegment(sketch, "E900", {"start": v(6.83, -7.23) * mm, "end": v(6.83, -6.33) * mm});
            skLineSegment(sketch, "E901", {"start": v(6.83, -6.33) * mm, "end": v(6.83, -5.43) * mm});
            skLineSegment(sketch, "E902", {"start": v(6.83, -5.43) * mm, "end": v(6.83, -4.52) * mm});
            skLineSegment(sketch, "E903", {"start": v(6.83, -4.52) * mm, "end": v(6.83, -3.62) * mm});
            skLineSegment(sketch, "E904", {"start": v(6.83, -3.62) * mm, "end": v(6.83, -2.72) * mm});
            skLineSegment(sketch, "E905", {"start": v(6.83, -2.72) * mm, "end": v(6.83, -1.81) * mm});
            skLineSegment(sketch, "E906", {"start": v(6.83, -1.81) * mm, "end": v(6.83, -0.9) * mm});
            skLineSegment(sketch, "E907", {"start": v(6.83, -0.9) * mm, "end": v(6.83, 0) * mm});
            skLineSegment(sketch, "E908", {"start": v(6.83, 0) * mm, "end": v(6.83, 0.9) * mm});
            skLineSegment(sketch, "E909", {"start": v(6.83, 0.9) * mm, "end": v(6.83, 1.8) * mm});
            skLineSegment(sketch, "E910", {"start": v(6.83, 1.8) * mm, "end": v(6.83, 2.7) * mm});
            skLineSegment(sketch, "E911", {"start": v(6.83, 2.7) * mm, "end": v(6.83, 3.6) * mm});
            skLineSegment(sketch, "E912", {"start": v(6.83, 3.6) * mm, "end": v(6.83, 4.51) * mm});
            skLineSegment(sketch, "E913", {"start": v(6.83, 4.51) * mm, "end": v(6.83, 5.42) * mm});
            skLineSegment(sketch, "E914", {"start": v(6.83, 5.42) * mm, "end": v(6.83, 6.32) * mm});
            skLineSegment(sketch, "E915", {"start": v(6.83, 6.32) * mm, "end": v(6.83, 7.22) * mm});
            skLineSegment(sketch, "E916.bottom", {"start": v(-46.12, 9.9) * mm, "end": v(45.54, 9.9) * mm});
            skLineSegment(sketch, "E916.top", {"start": v(-46.12, -10.3) * mm, "end": v(45.54, -10.3) * mm});
            skLineSegment(sketch, "E916.left", {"start": v(-46.12, 9.9) * mm, "end": v(-46.12, -10.3) * mm});
            skLineSegment(sketch, "E916.right", {"start": v(45.54, 9.9) * mm, "end": v(45.54, -10.3) * mm});
            skSolve(sketch);
        }
        {
            var Q0;
            Q0=makeQuery(id+"F0.imprint","IMPRINT",FACE,{"disambiguationData":[TD([[makeQuery(id+"F0.imprint","IMPRINT",EDGE,{"derivedFrom":sQuery(id+"F0.wireOp",EDGE,"E0")}),-1.0]])]});
            var Q1;
            Q1=makeQuery(id+"F0.imprint","IMPRINT",FACE,{"disambiguationData":[TD([[makeQuery(id+"F0.imprint","IMPRINT",EDGE,{"derivedFrom":sQuery(id+"F0.wireOp",EDGE,"E96")}),-1.0]])]});
            var Q2;
            Q2=makeQuery(id+"F0.imprint","IMPRINT",FACE,{"disambiguationData":[TD([[makeQuery(id+"F0.imprint","IMPRINT",EDGE,{"derivedFrom":sQuery(id+"F0.wireOp",EDGE,"E610")}),1.0]])]});
            var Q3;
            Q3=makeQuery(id+"F0.imprint","IMPRINT",FACE,{"disambiguationData":[TD([[makeQuery(id+"F0.imprint","IMPRINT",EDGE,{"derivedFrom":sQuery(id+"F0.wireOp",EDGE,"E852")}),1.0]])]});
            var Q4;
            Q4=makeQuery(id+"F0.imprint","IMPRINT",FACE,{"disambiguationData":[TD([[makeQuery(id+"F0.imprint","IMPRINT",EDGE,{"derivedFrom":sQuery(id+"F0.wireOp",EDGE,"E288")}),-1.0]])]});
            var Q5;
            Q5=makeQuery(id+"F0.imprint","IMPRINT",FACE,{"disambiguationData":[TD([[makeQuery(id+"F0.imprint","IMPRINT",EDGE,{"derivedFrom":sQuery(id+"F0.wireOp",EDGE,"E450")}),-1.0]])]});
            extrude(context, id + "F1", {"entities" : qUnion([Q0, Q1, Q2, Q3, Q4, Q5]), "depth" : 5 * mm, "offsetDistance" : 25 * mm});
        }
        {
            var Q0;
            Q0=makeQuery(id+"F0.imprint","IMPRINT",FACE,{"disambiguationData":[TD([[makeQuery(id+"F0.imprint","IMPRINT",EDGE,{"derivedFrom":sQuery(id+"F0.wireOp",EDGE,"E0")}),1.0]])]});
            var Q1;
            Q1=makeQuery(id+"F0.imprint","IMPRINT",FACE,{"disambiguationData":[TD([[makeQuery(id+"F0.imprint","IMPRINT",EDGE,{"derivedFrom":sQuery(id+"F0.wireOp",EDGE,"E0")}),-1.0]])]});
            var Q2;
            Q2=makeQuery(id+"F0.imprint","IMPRINT",FACE,{"disambiguationData":[TD([[makeQuery(id+"F0.imprint","IMPRINT",EDGE,{"derivedFrom":sQuery(id+"F0.wireOp",EDGE,"E96")}),-1.0]])]});
            var Q3;
            Q3=makeQuery(id+"F0.imprint","IMPRINT",FACE,{"disambiguationData":[TD([[makeQuery(id+"F0.imprint","IMPRINT",EDGE,{"derivedFrom":sQuery(id+"F0.wireOp",EDGE,"E610")}),1.0]])]});
            var Q4;
            Q4=makeQuery(id+"F0.imprint","IMPRINT",FACE,{"disambiguationData":[TD([[makeQuery(id+"F0.imprint","IMPRINT",EDGE,{"derivedFrom":sQuery(id+"F0.wireOp",EDGE,"E852")}),1.0]])]});
            var Q5;
            Q5=makeQuery(id+"F0.imprint","IMPRINT",FACE,{"disambiguationData":[TD([[makeQuery(id+"F0.imprint","IMPRINT",EDGE,{"derivedFrom":sQuery(id+"F0.wireOp",EDGE,"E288")}),-1.0]])]});
            var Q6;
            Q6=makeQuery(id+"F0.imprint","IMPRINT",FACE,{"disambiguationData":[TD([[makeQuery(id+"F0.imprint","IMPRINT",EDGE,{"derivedFrom":sQuery(id+"F0.wireOp",EDGE,"E450")}),-1.0]])]});
            var Q7;
            Q7=makeQuery(id+"F0.imprint","IMPRINT",FACE,{"disambiguationData":[TD([[makeQuery(id+"F0.imprint","IMPRINT",EDGE,{"derivedFrom":sQuery(id+"F0.wireOp",EDGE,"E288")}),1.0]])]});
            extrude(context, id + "F2", {"entities" : qUnion([Q0, Q1, Q2, Q3, Q4, Q5, Q6, Q7]), "oppositeDirection" : true, "depth" : 0.5 * mm, "offsetDistance" : 25 * mm});
        }
    });
